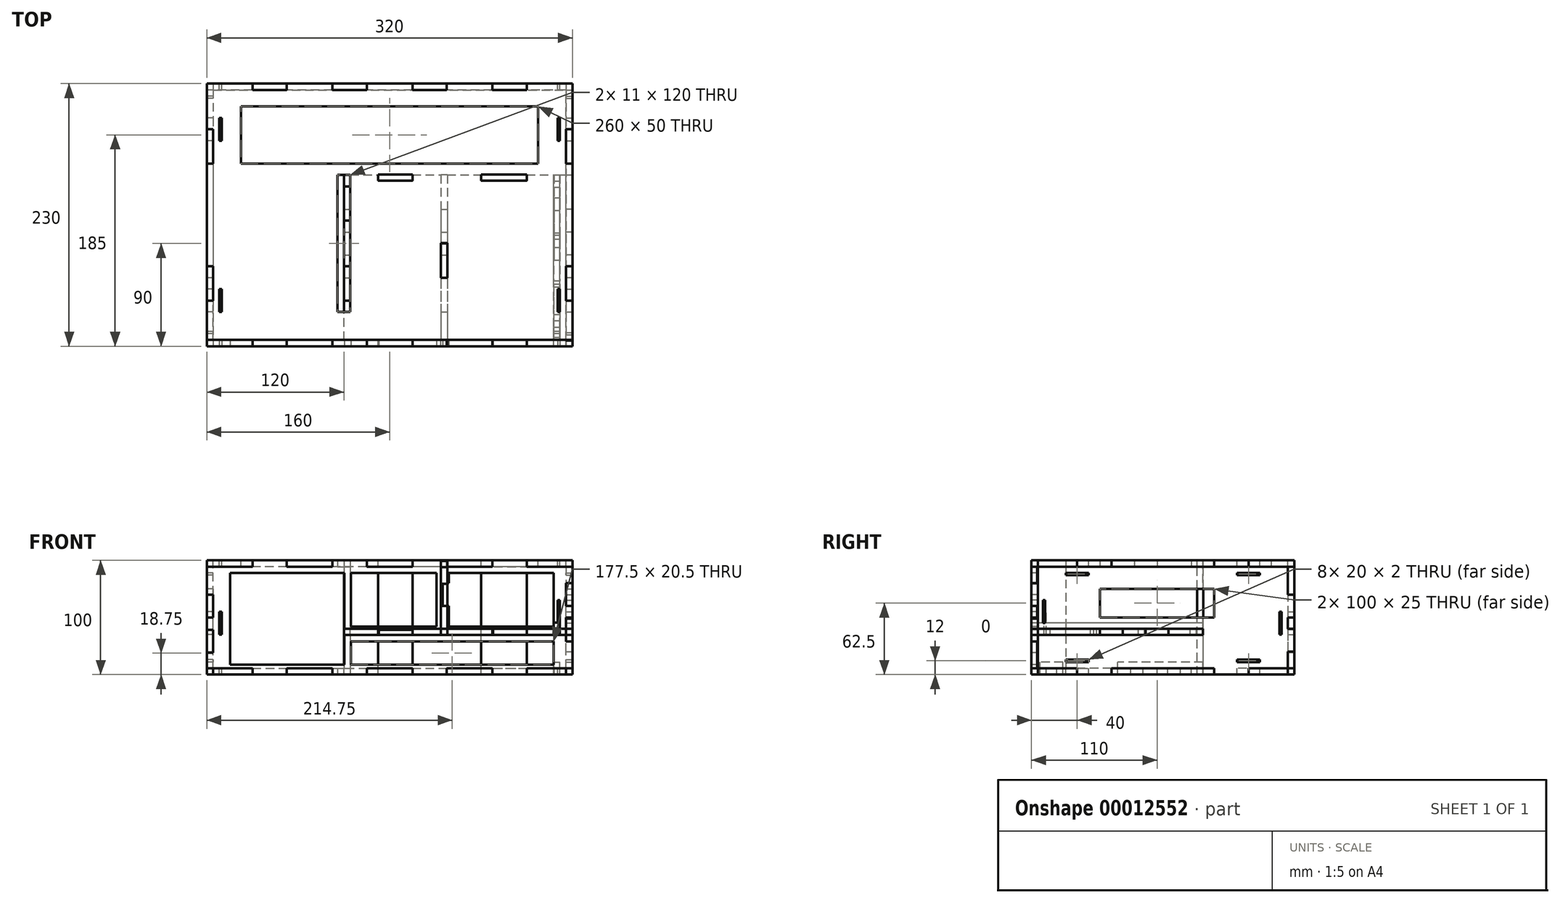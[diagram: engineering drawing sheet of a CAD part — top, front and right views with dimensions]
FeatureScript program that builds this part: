
annotation { "Feature Type Name" : "Feature", "Feature Type Description" : "" }
export const myFeature = defineFeature(function(context is Context, id is Id, definition is map)
    precondition{}
    {
        {
            var Q0;
            Q0=qCreatedBy(makeId("Top.planeOp"),FACE);
            var sketch = newSketch(context, id + "F0", { "sketchPlane" : qUnion([Q0])});
            skLineSegment(sketch, "E0.bottom", {"start": v(0, 0) * mm, "end": v(-320, 0) * mm});
            skLineSegment(sketch, "E0.top", {"start": v(0, 230) * mm, "end": v(-320, 230) * mm});
            skLineSegment(sketch, "E0.left", {"start": v(0, 0) * mm, "end": v(0, 230) * mm});
            skLineSegment(sketch, "E0.right", {"start": v(-320, 0) * mm, "end": v(-320, 230) * mm});
            skSolve(sketch);
        }
        {
            var Q0;
            Q0 = qSketchRegion(id + "F0", true);
            extrude(context, id + "F1", {"entities" : qUnion([Q0]), "depth" : 5.5 * mm});
        }
        {
            var Q0;
            Q0=makeQuery(id+"F1.opExtrude","CAP_FACE",FACE,{"disambiguationData":[OSD([sQuery(id+"F0.wireOp",EDGE,"E0.bottom"),sQuery(id+"F0.wireOp",EDGE,"E0.top"),sQuery(id+"F0.wireOp",EDGE,"E0.left"),sQuery(id+"F0.wireOp",EDGE,"E0.right")])],"isStart":false});
            var sketch = newSketch(context, id + "F2", { "sketchPlane" : qUnion([Q0])});
            skLineSegment(sketch, "E1.bottom", {"start": v(-280, 230) * mm, "end": v(-250, 230) * mm});
            skLineSegment(sketch, "E1.top", {"start": v(-280, 224.5) * mm, "end": v(-250, 224.5) * mm});
            skLineSegment(sketch, "E1.left", {"start": v(-280, 230) * mm, "end": v(-280, 224.5) * mm});
            skLineSegment(sketch, "E1.right", {"start": v(-250, 230) * mm, "end": v(-250, 224.5) * mm});
            skLineSegment(sketch, "E2.bottom", {"start": v(-70, 230) * mm, "end": v(-40, 230) * mm});
            skLineSegment(sketch, "E2.top", {"start": v(-70, 224.5) * mm, "end": v(-40, 224.5) * mm});
            skLineSegment(sketch, "E2.left", {"start": v(-70, 230) * mm, "end": v(-70, 224.5) * mm});
            skLineSegment(sketch, "E2.right", {"start": v(-40, 230) * mm, "end": v(-40, 224.5) * mm});
            skLineSegment(sketch, "E3.bottom", {"start": v(0, 190) * mm, "end": v(-5.5, 190) * mm});
            skLineSegment(sketch, "E3.top", {"start": v(0, 160) * mm, "end": v(-5.5, 160) * mm});
            skLineSegment(sketch, "E3.left", {"start": v(0, 190) * mm, "end": v(0, 160) * mm});
            skLineSegment(sketch, "E3.right", {"start": v(-5.5, 190) * mm, "end": v(-5.5, 160) * mm});
            skLineSegment(sketch, "E4.bottom", {"start": v(0, 70) * mm, "end": v(-5.5, 70) * mm});
            skLineSegment(sketch, "E4.top", {"start": v(0, 40) * mm, "end": v(-5.5, 40) * mm});
            skLineSegment(sketch, "E4.left", {"start": v(0, 70) * mm, "end": v(0, 40) * mm});
            skLineSegment(sketch, "E4.right", {"start": v(-5.5, 70) * mm, "end": v(-5.5, 40) * mm});
            skLineSegment(sketch, "E5.bottom", {"start": v(-320, 190) * mm, "end": v(-314.5, 190) * mm});
            skLineSegment(sketch, "E5.top", {"start": v(-320, 160) * mm, "end": v(-314.5, 160) * mm});
            skLineSegment(sketch, "E5.left", {"start": v(-320, 190) * mm, "end": v(-320, 160) * mm});
            skLineSegment(sketch, "E5.right", {"start": v(-314.5, 190) * mm, "end": v(-314.5, 160) * mm});
            skLineSegment(sketch, "E6.bottom", {"start": v(-320, 70) * mm, "end": v(-314.5, 70) * mm});
            skLineSegment(sketch, "E6.top", {"start": v(-320, 40) * mm, "end": v(-314.5, 40) * mm});
            skLineSegment(sketch, "E6.left", {"start": v(-320, 70) * mm, "end": v(-320, 40) * mm});
            skLineSegment(sketch, "E6.right", {"start": v(-314.5, 70) * mm, "end": v(-314.5, 40) * mm});
            skLineSegment(sketch, "E7.bottom", {"start": v(-210, 230) * mm, "end": v(-180, 230) * mm});
            skLineSegment(sketch, "E7.top", {"start": v(-210, 224.5) * mm, "end": v(-180, 224.5) * mm});
            skLineSegment(sketch, "E7.left", {"start": v(-210, 230) * mm, "end": v(-210, 224.5) * mm});
            skLineSegment(sketch, "E7.right", {"start": v(-180, 230) * mm, "end": v(-180, 224.5) * mm});
            skLineSegment(sketch, "E8.bottom", {"start": v(-140, 230) * mm, "end": v(-110, 230) * mm});
            skLineSegment(sketch, "E8.top", {"start": v(-140, 224.5) * mm, "end": v(-110, 224.5) * mm});
            skLineSegment(sketch, "E8.left", {"start": v(-140, 230) * mm, "end": v(-140, 224.5) * mm});
            skLineSegment(sketch, "E8.right", {"start": v(-110, 230) * mm, "end": v(-110, 224.5) * mm});
            skLineSegment(sketch, "E9.bottom", {"start": v(-309, 30) * mm, "end": v(-307, 30) * mm});
            skLineSegment(sketch, "E9.top", {"start": v(-309, 50) * mm, "end": v(-307, 50) * mm});
            skLineSegment(sketch, "E9.left", {"start": v(-309, 30) * mm, "end": v(-309, 50) * mm});
            skLineSegment(sketch, "E9.right", {"start": v(-307, 30) * mm, "end": v(-307, 50) * mm});
            skLineSegment(sketch, "E10.bottom", {"start": v(-13, 30) * mm, "end": v(-11, 30) * mm});
            skLineSegment(sketch, "E10.top", {"start": v(-13, 50) * mm, "end": v(-11, 50) * mm});
            skLineSegment(sketch, "E10.left", {"start": v(-13, 30) * mm, "end": v(-13, 50) * mm});
            skLineSegment(sketch, "E10.right", {"start": v(-11, 30) * mm, "end": v(-11, 50) * mm});
            skLineSegment(sketch, "E11.bottom", {"start": v(-11, 200) * mm, "end": v(-13, 200) * mm});
            skLineSegment(sketch, "E11.top", {"start": v(-11, 180) * mm, "end": v(-13, 180) * mm});
            skLineSegment(sketch, "E11.left", {"start": v(-11, 200) * mm, "end": v(-11, 180) * mm});
            skLineSegment(sketch, "E11.right", {"start": v(-13, 200) * mm, "end": v(-13, 180) * mm});
            skLineSegment(sketch, "E12.bottom", {"start": v(-309, 200) * mm, "end": v(-307, 200) * mm});
            skLineSegment(sketch, "E12.top", {"start": v(-309, 180) * mm, "end": v(-307, 180) * mm});
            skLineSegment(sketch, "E12.left", {"start": v(-309, 200) * mm, "end": v(-309, 180) * mm});
            skLineSegment(sketch, "E12.right", {"start": v(-307, 200) * mm, "end": v(-307, 180) * mm});
            skLineSegment(sketch, "E13.bottom", {"start": v(-280, 0) * mm, "end": v(-250, 0) * mm});
            skLineSegment(sketch, "E13.top", {"start": v(-280, 5.5) * mm, "end": v(-250, 5.5) * mm});
            skLineSegment(sketch, "E13.left", {"start": v(-280, 0) * mm, "end": v(-280, 5.5) * mm});
            skLineSegment(sketch, "E13.right", {"start": v(-250, 0) * mm, "end": v(-250, 5.5) * mm});
            skLineSegment(sketch, "E14.bottom", {"start": v(-210, 0) * mm, "end": v(-180, 0) * mm});
            skLineSegment(sketch, "E14.top", {"start": v(-210, 5.5) * mm, "end": v(-180, 5.5) * mm});
            skLineSegment(sketch, "E14.left", {"start": v(-210, 0) * mm, "end": v(-210, 5.5) * mm});
            skLineSegment(sketch, "E14.right", {"start": v(-180, 0) * mm, "end": v(-180, 5.5) * mm});
            skLineSegment(sketch, "E15.bottom", {"start": v(-140, 0) * mm, "end": v(-110, 0) * mm});
            skLineSegment(sketch, "E15.top", {"start": v(-140, 5.5) * mm, "end": v(-110, 5.5) * mm});
            skLineSegment(sketch, "E15.left", {"start": v(-140, 0) * mm, "end": v(-140, 5.5) * mm});
            skLineSegment(sketch, "E15.right", {"start": v(-110, 0) * mm, "end": v(-110, 5.5) * mm});
            skLineSegment(sketch, "E16.bottom", {"start": v(-70, 0) * mm, "end": v(-40, 0) * mm});
            skLineSegment(sketch, "E16.top", {"start": v(-70, 5.5) * mm, "end": v(-40, 5.5) * mm});
            skLineSegment(sketch, "E16.left", {"start": v(-70, 0) * mm, "end": v(-70, 5.5) * mm});
            skLineSegment(sketch, "E16.right", {"start": v(-40, 0) * mm, "end": v(-40, 5.5) * mm});
            skLineSegment(sketch, "E17.bottom", {"start": v(-200, 140) * mm, "end": v(-194.5, 140) * mm});
            skLineSegment(sketch, "E17.top", {"start": v(-200, 110) * mm, "end": v(-194.5, 110) * mm});
            skLineSegment(sketch, "E17.left", {"start": v(-200, 140) * mm, "end": v(-200, 110) * mm});
            skLineSegment(sketch, "E17.right", {"start": v(-194.5, 140) * mm, "end": v(-194.5, 110) * mm});
            skLineSegment(sketch, "E18.bottom", {"start": v(-200, 70) * mm, "end": v(-194.5, 70) * mm});
            skLineSegment(sketch, "E18.top", {"start": v(-200, 40) * mm, "end": v(-194.5, 40) * mm});
            skLineSegment(sketch, "E18.left", {"start": v(-200, 70) * mm, "end": v(-200, 40) * mm});
            skLineSegment(sketch, "E18.right", {"start": v(-194.5, 70) * mm, "end": v(-194.5, 40) * mm});
            skLineSegment(sketch, "E19.bottom", {"start": v(-170, 150.5) * mm, "end": v(-140, 150.5) * mm});
            skLineSegment(sketch, "E19.top", {"start": v(-170, 145) * mm, "end": v(-140, 145) * mm});
            skLineSegment(sketch, "E19.left", {"start": v(-170, 150.5) * mm, "end": v(-170, 145) * mm});
            skLineSegment(sketch, "E19.right", {"start": v(-140, 150.5) * mm, "end": v(-140, 145) * mm});
            skLineSegment(sketch, "E20.bottom", {"start": v(-80, 150.5) * mm, "end": v(-40, 150.5) * mm});
            skLineSegment(sketch, "E20.top", {"start": v(-80, 145) * mm, "end": v(-40, 145) * mm});
            skLineSegment(sketch, "E20.left", {"start": v(-80, 150.5) * mm, "end": v(-80, 145) * mm});
            skLineSegment(sketch, "E20.right", {"start": v(-40, 150.5) * mm, "end": v(-40, 145) * mm});
            skLineSegment(sketch, "E21.bottom", {"start": v(-16.5, 130) * mm, "end": v(-11, 130) * mm});
            skLineSegment(sketch, "E21.top", {"start": v(-16.5, 119) * mm, "end": v(-11, 119) * mm});
            skLineSegment(sketch, "E21.left", {"start": v(-16.5, 130) * mm, "end": v(-16.5, 119) * mm});
            skLineSegment(sketch, "E21.right", {"start": v(-11, 130) * mm, "end": v(-11, 119) * mm});
            skLineSegment(sketch, "E22.bottom", {"start": v(-16.5, 97.5) * mm, "end": v(-11, 97.5) * mm});
            skLineSegment(sketch, "E22.top", {"start": v(-16.5, 86.5) * mm, "end": v(-11, 86.5) * mm});
            skLineSegment(sketch, "E22.left", {"start": v(-16.5, 97.5) * mm, "end": v(-16.5, 86.5) * mm});
            skLineSegment(sketch, "E22.right", {"start": v(-11, 97.5) * mm, "end": v(-11, 86.5) * mm});
            skLineSegment(sketch, "E23.bottom", {"start": v(-16.5, 22) * mm, "end": v(-11, 22) * mm});
            skLineSegment(sketch, "E23.top", {"start": v(-16.5, 11) * mm, "end": v(-11, 11) * mm});
            skLineSegment(sketch, "E23.left", {"start": v(-16.5, 22) * mm, "end": v(-16.5, 11) * mm});
            skLineSegment(sketch, "E23.right", {"start": v(-11, 22) * mm, "end": v(-11, 11) * mm});
            skSolve(sketch);
        }
        {
            var Q0;
            Q0 = qSketchRegion(id + "F2", true);
            extrude(context, id + "F3", {"entities" : qUnion([Q0]), "operationType" : NewBodyOperationType.REMOVE, "oppositeDirection" : true, "depth" : 5.5 * mm});
        }
        {
            var Q0;
            {var subQ0=sQuery(id+"F0.wireOp",EDGE,"E0.top");Q0=makeQuery(id+"F3.boolean.opBoolean","SPLIT",FACE,{"disambiguationData":[TD([makeQuery(id+"F3.opExtrude","SWEPT_FACE",FACE,{"disambiguationData":[OSD([sQuery(id+"F2.wireOp",EDGE,"E2.left")])]})])],"derivedFrom":makeQuery(id+"F1.opExtrude","SWEPT_FACE",FACE,{"disambiguationData":[OSD([subQ0])]})});}
            var sketch = newSketch(context, id + "F4", { "sketchPlane" : qUnion([Q0])});
            skLineSegment(sketch, "E24.bottom", {"start": v(320, 0) * mm, "end": v(0, 0) * mm});
            skLineSegment(sketch, "E24.top", {"start": v(320, 100) * mm, "end": v(0, 100) * mm});
            skLineSegment(sketch, "E24.left", {"start": v(320, 0) * mm, "end": v(320, 100) * mm});
            skLineSegment(sketch, "E24.right", {"start": v(0, 0) * mm, "end": v(0, 100) * mm});
            skSolve(sketch);
        }
        {
            var Q0;
            Q0 = qSketchRegion(id + "F4", true);
            extrude(context, id + "F5", {"entities" : qUnion([Q0]), "oppositeDirection" : true, "depth" : 5.5 * mm});
        }
        {
            var Q0;
            Q0=makeQuery(id+"F5.opExtrude","CAP_FACE",FACE,{"disambiguationData":[OSD([sQuery(id+"F4.wireOp",EDGE,"E24.bottom"),sQuery(id+"F4.wireOp",EDGE,"E24.top"),sQuery(id+"F4.wireOp",EDGE,"E24.left"),sQuery(id+"F4.wireOp",EDGE,"E24.right")])],"isStart":true});
            var sketch = newSketch(context, id + "F6", { "sketchPlane" : qUnion([Q0])});
            skLineSegment(sketch, "E25.bottom", {"start": v(0, 0) * mm, "end": v(40, 0) * mm});
            skLineSegment(sketch, "E25.top", {"start": v(0, 5.5) * mm, "end": v(40, 5.5) * mm});
            skLineSegment(sketch, "E25.left", {"start": v(0, 0) * mm, "end": v(0, 5.5) * mm});
            skLineSegment(sketch, "E25.right", {"start": v(40, 0) * mm, "end": v(40, 5.5) * mm});
            skLineSegment(sketch, "E26.bottom", {"start": v(70, 0) * mm, "end": v(110, 0) * mm});
            skLineSegment(sketch, "E26.top", {"start": v(70, 5.5) * mm, "end": v(110, 5.5) * mm});
            skLineSegment(sketch, "E26.left", {"start": v(70, 0) * mm, "end": v(70, 5.5) * mm});
            skLineSegment(sketch, "E26.right", {"start": v(110, 0) * mm, "end": v(110, 5.5) * mm});
            skLineSegment(sketch, "E27.bottom", {"start": v(140, 0) * mm, "end": v(180, 0) * mm});
            skLineSegment(sketch, "E27.top", {"start": v(140, 5.5) * mm, "end": v(180, 5.5) * mm});
            skLineSegment(sketch, "E27.left", {"start": v(140, 0) * mm, "end": v(140, 5.5) * mm});
            skLineSegment(sketch, "E27.right", {"start": v(180, 0) * mm, "end": v(180, 5.5) * mm});
            skLineSegment(sketch, "E28.bottom", {"start": v(210, 0) * mm, "end": v(250, 0) * mm});
            skLineSegment(sketch, "E28.top", {"start": v(210, 5.5) * mm, "end": v(250, 5.5) * mm});
            skLineSegment(sketch, "E28.left", {"start": v(210, 0) * mm, "end": v(210, 5.5) * mm});
            skLineSegment(sketch, "E28.right", {"start": v(250, 0) * mm, "end": v(250, 5.5) * mm});
            skLineSegment(sketch, "E29.bottom", {"start": v(280, 0) * mm, "end": v(320, 0) * mm});
            skLineSegment(sketch, "E29.top", {"start": v(280, 5.5) * mm, "end": v(320, 5.5) * mm});
            skLineSegment(sketch, "E29.left", {"start": v(280, 0) * mm, "end": v(280, 5.5) * mm});
            skLineSegment(sketch, "E29.right", {"start": v(320, 0) * mm, "end": v(320, 5.5) * mm});
            skLineSegment(sketch, "E30.bottom", {"start": v(0, 70) * mm, "end": v(5.5, 70) * mm});
            skLineSegment(sketch, "E30.top", {"start": v(0, 50) * mm, "end": v(5.5, 50) * mm});
            skLineSegment(sketch, "E30.left", {"start": v(0, 70) * mm, "end": v(0, 50) * mm});
            skLineSegment(sketch, "E30.right", {"start": v(5.5, 70) * mm, "end": v(5.5, 50) * mm});
            skLineSegment(sketch, "E31.bottom", {"start": v(0, 40) * mm, "end": v(5.5, 40) * mm});
            skLineSegment(sketch, "E31.top", {"start": v(0, 20) * mm, "end": v(5.5, 20) * mm});
            skLineSegment(sketch, "E31.left", {"start": v(0, 40) * mm, "end": v(0, 20) * mm});
            skLineSegment(sketch, "E31.right", {"start": v(5.5, 40) * mm, "end": v(5.5, 20) * mm});
            skLineSegment(sketch, "E32.bottom", {"start": v(11, 55) * mm, "end": v(13, 55) * mm});
            skLineSegment(sketch, "E32.top", {"start": v(11, 35) * mm, "end": v(13, 35) * mm});
            skLineSegment(sketch, "E32.left", {"start": v(11, 55) * mm, "end": v(11, 35) * mm});
            skLineSegment(sketch, "E32.right", {"start": v(13, 55) * mm, "end": v(13, 35) * mm});
            skLineSegment(sketch, "E33.bottom", {"start": v(0, 100) * mm, "end": v(40, 100) * mm});
            skLineSegment(sketch, "E33.top", {"start": v(0, 94.5) * mm, "end": v(40, 94.5) * mm});
            skLineSegment(sketch, "E33.left", {"start": v(0, 100) * mm, "end": v(0, 94.5) * mm});
            skLineSegment(sketch, "E33.right", {"start": v(40, 100) * mm, "end": v(40, 94.5) * mm});
            skLineSegment(sketch, "E34.bottom", {"start": v(70, 100) * mm, "end": v(110, 100) * mm});
            skLineSegment(sketch, "E34.top", {"start": v(70, 94.5) * mm, "end": v(110, 94.5) * mm});
            skLineSegment(sketch, "E34.left", {"start": v(70, 100) * mm, "end": v(70, 94.5) * mm});
            skLineSegment(sketch, "E34.right", {"start": v(110, 100) * mm, "end": v(110, 94.5) * mm});
            skLineSegment(sketch, "E35.bottom", {"start": v(140, 100) * mm, "end": v(180, 100) * mm});
            skLineSegment(sketch, "E35.top", {"start": v(140, 94.5) * mm, "end": v(180, 94.5) * mm});
            skLineSegment(sketch, "E35.left", {"start": v(140, 100) * mm, "end": v(140, 94.5) * mm});
            skLineSegment(sketch, "E35.right", {"start": v(180, 100) * mm, "end": v(180, 94.5) * mm});
            skLineSegment(sketch, "E36.bottom", {"start": v(210, 100) * mm, "end": v(250, 100) * mm});
            skLineSegment(sketch, "E36.top", {"start": v(210, 94.5) * mm, "end": v(250, 94.5) * mm});
            skLineSegment(sketch, "E36.left", {"start": v(210, 100) * mm, "end": v(210, 94.5) * mm});
            skLineSegment(sketch, "E36.right", {"start": v(250, 100) * mm, "end": v(250, 94.5) * mm});
            skLineSegment(sketch, "E37.bottom", {"start": v(280, 100) * mm, "end": v(320, 100) * mm});
            skLineSegment(sketch, "E37.top", {"start": v(280, 94.5) * mm, "end": v(320, 94.5) * mm});
            skLineSegment(sketch, "E37.left", {"start": v(280, 100) * mm, "end": v(280, 94.5) * mm});
            skLineSegment(sketch, "E37.right", {"start": v(320, 100) * mm, "end": v(320, 94.5) * mm});
            skLineSegment(sketch, "E38.bottom", {"start": v(320, 70) * mm, "end": v(314.5, 70) * mm});
            skLineSegment(sketch, "E38.top", {"start": v(320, 50) * mm, "end": v(314.5, 50) * mm});
            skLineSegment(sketch, "E38.left", {"start": v(320, 70) * mm, "end": v(320, 50) * mm});
            skLineSegment(sketch, "E38.right", {"start": v(314.5, 70) * mm, "end": v(314.5, 50) * mm});
            skLineSegment(sketch, "E39.bottom", {"start": v(320, 40) * mm, "end": v(314.5, 40) * mm});
            skLineSegment(sketch, "E39.top", {"start": v(320, 20) * mm, "end": v(314.5, 20) * mm});
            skLineSegment(sketch, "E39.left", {"start": v(320, 40) * mm, "end": v(320, 20) * mm});
            skLineSegment(sketch, "E39.right", {"start": v(314.5, 40) * mm, "end": v(314.5, 20) * mm});
            skLineSegment(sketch, "E40.bottom", {"start": v(309, 55) * mm, "end": v(307, 55) * mm});
            skLineSegment(sketch, "E40.top", {"start": v(309, 35) * mm, "end": v(307, 35) * mm});
            skLineSegment(sketch, "E40.left", {"start": v(309, 55) * mm, "end": v(309, 35) * mm});
            skLineSegment(sketch, "E40.right", {"start": v(307, 55) * mm, "end": v(307, 35) * mm});
            skSolve(sketch);
        }
        {
            var Q0;
            Q0 = qSketchRegion(id + "F6", true);
            extrude(context, id + "F7", {"entities" : qUnion([Q0]), "operationType" : NewBodyOperationType.REMOVE, "oppositeDirection" : true, "depth" : 5.5 * mm});
        }
        {
            var Q0;
            {var subQ0=sQuery(id+"F0.wireOp",EDGE,"E0.left");var subQ1=sQuery(id+"F0.wireOp",EDGE,"E0.top");Q0=makeQuery(id+"F3.boolean.opBoolean","SPLIT",FACE,{"disambiguationData":[TD([makeQuery(id+"F1.opExtrude","SWEPT_FACE",FACE,{"disambiguationData":[OSD([subQ1])]})])],"derivedFrom":makeQuery(id+"F1.opExtrude","SWEPT_FACE",FACE,{"disambiguationData":[OSD([subQ0])]})});}
            var sketch = newSketch(context, id + "F8", { "sketchPlane" : qUnion([Q0])});
            skLineSegment(sketch, "E41.bottom", {"start": v(230, 0) * mm, "end": v(0, 0) * mm});
            skLineSegment(sketch, "E41.top", {"start": v(230, 100) * mm, "end": v(0, 100) * mm});
            skLineSegment(sketch, "E41.left", {"start": v(230, 0) * mm, "end": v(230, 100) * mm});
            skLineSegment(sketch, "E41.right", {"start": v(0, 0) * mm, "end": v(0, 100) * mm});
            skSolve(sketch);
        }
        {
            var Q0;
            Q0 = qSketchRegion(id + "F8", true);
            extrude(context, id + "F9", {"entities" : qUnion([Q0]), "oppositeDirection" : true, "depth" : 5.5 * mm});
        }
        {
            var Q0;
            Q0=makeQuery(id+"F9.opExtrude","CAP_FACE",FACE,{"disambiguationData":[OSD([sQuery(id+"F8.wireOp",EDGE,"E41.bottom"),sQuery(id+"F8.wireOp",EDGE,"E41.top"),sQuery(id+"F8.wireOp",EDGE,"E41.left"),sQuery(id+"F8.wireOp",EDGE,"E41.right")])],"isStart":true});
            var sketch = newSketch(context, id + "F10", { "sketchPlane" : qUnion([Q0])});
            skLineSegment(sketch, "E42.bottom", {"start": v(230, 100) * mm, "end": v(224.5, 100) * mm});
            skLineSegment(sketch, "E42.top", {"start": v(230, 70) * mm, "end": v(224.5, 70) * mm});
            skLineSegment(sketch, "E42.left", {"start": v(230, 100) * mm, "end": v(230, 70) * mm});
            skLineSegment(sketch, "E42.right", {"start": v(224.5, 100) * mm, "end": v(224.5, 70) * mm});
            skLineSegment(sketch, "E43.bottom", {"start": v(230, 50) * mm, "end": v(224.5, 50) * mm});
            skLineSegment(sketch, "E43.top", {"start": v(230, 40) * mm, "end": v(224.5, 40) * mm});
            skLineSegment(sketch, "E43.left", {"start": v(230, 50) * mm, "end": v(230, 40) * mm});
            skLineSegment(sketch, "E43.right", {"start": v(224.5, 50) * mm, "end": v(224.5, 40) * mm});
            skLineSegment(sketch, "E44.bottom", {"start": v(230, 0) * mm, "end": v(190, 0) * mm});
            skLineSegment(sketch, "E44.top", {"start": v(230, 5.5) * mm, "end": v(190, 5.5) * mm});
            skLineSegment(sketch, "E44.left", {"start": v(230, 0) * mm, "end": v(230, 5.5) * mm});
            skLineSegment(sketch, "E44.right", {"start": v(190, 0) * mm, "end": v(190, 5.5) * mm});
            skLineSegment(sketch, "E45.bottom", {"start": v(160, 0) * mm, "end": v(70, 0) * mm});
            skLineSegment(sketch, "E45.top", {"start": v(160, 5.5) * mm, "end": v(70, 5.5) * mm});
            skLineSegment(sketch, "E45.left", {"start": v(160, 0) * mm, "end": v(160, 5.5) * mm});
            skLineSegment(sketch, "E45.right", {"start": v(70, 0) * mm, "end": v(70, 5.5) * mm});
            skLineSegment(sketch, "E46.bottom", {"start": v(0, 0) * mm, "end": v(40, 0) * mm});
            skLineSegment(sketch, "E46.top", {"start": v(0, 5.5) * mm, "end": v(40, 5.5) * mm});
            skLineSegment(sketch, "E46.left", {"start": v(0, 0) * mm, "end": v(0, 5.5) * mm});
            skLineSegment(sketch, "E46.right", {"start": v(40, 0) * mm, "end": v(40, 5.5) * mm});
            skLineSegment(sketch, "E47.bottom", {"start": v(230, 5.5) * mm, "end": v(224.5, 5.5) * mm});
            skLineSegment(sketch, "E47.top", {"start": v(230, 20) * mm, "end": v(224.5, 20) * mm});
            skLineSegment(sketch, "E47.left", {"start": v(230, 5.5) * mm, "end": v(230, 20) * mm});
            skLineSegment(sketch, "E47.right", {"start": v(224.5, 5.5) * mm, "end": v(224.5, 20) * mm});
            skLineSegment(sketch, "E48.bottom", {"start": v(0, 5.5) * mm, "end": v(5, 5.5) * mm});
            skLineSegment(sketch, "E48.top", {"start": v(0, 30) * mm, "end": v(5, 30) * mm});
            skLineSegment(sketch, "E48.left", {"start": v(0, 5.5) * mm, "end": v(0, 30) * mm});
            skLineSegment(sketch, "E48.right", {"start": v(5, 5.5) * mm, "end": v(5, 30) * mm});
            skLineSegment(sketch, "E49.bottom", {"start": v(0, 50) * mm, "end": v(5, 50) * mm});
            skLineSegment(sketch, "E49.top", {"start": v(0, 60) * mm, "end": v(5, 60) * mm});
            skLineSegment(sketch, "E49.left", {"start": v(0, 50) * mm, "end": v(0, 60) * mm});
            skLineSegment(sketch, "E49.right", {"start": v(5, 50) * mm, "end": v(5, 60) * mm});
            skLineSegment(sketch, "E50.bottom", {"start": v(0, 100) * mm, "end": v(5, 100) * mm});
            skLineSegment(sketch, "E50.top", {"start": v(0, 80) * mm, "end": v(5, 80) * mm});
            skLineSegment(sketch, "E50.left", {"start": v(0, 100) * mm, "end": v(0, 80) * mm});
            skLineSegment(sketch, "E50.right", {"start": v(5, 100) * mm, "end": v(5, 80) * mm});
            skLineSegment(sketch, "E51.bottom", {"start": v(217, 35) * mm, "end": v(219, 35) * mm});
            skLineSegment(sketch, "E51.top", {"start": v(217, 55) * mm, "end": v(219, 55) * mm});
            skLineSegment(sketch, "E51.left", {"start": v(217, 35) * mm, "end": v(217, 55) * mm});
            skLineSegment(sketch, "E51.right", {"start": v(219, 35) * mm, "end": v(219, 55) * mm});
            skLineSegment(sketch, "E52.bottom", {"start": v(12, 45) * mm, "end": v(10, 45) * mm});
            skLineSegment(sketch, "E52.top", {"start": v(12, 65) * mm, "end": v(10, 65) * mm});
            skLineSegment(sketch, "E52.left", {"start": v(12, 45) * mm, "end": v(12, 65) * mm});
            skLineSegment(sketch, "E52.right", {"start": v(10, 45) * mm, "end": v(10, 65) * mm});
            skLineSegment(sketch, "E53.bottom", {"start": v(5, 94.5) * mm, "end": v(40, 94.5) * mm});
            skLineSegment(sketch, "E53.top", {"start": v(5, 100) * mm, "end": v(40, 100) * mm});
            skLineSegment(sketch, "E53.left", {"start": v(5, 94.5) * mm, "end": v(5, 100) * mm});
            skLineSegment(sketch, "E53.right", {"start": v(40, 94.5) * mm, "end": v(40, 100) * mm});
            skLineSegment(sketch, "E54.bottom", {"start": v(70, 100) * mm, "end": v(160, 100) * mm});
            skLineSegment(sketch, "E54.top", {"start": v(70, 94.5) * mm, "end": v(160, 94.5) * mm});
            skLineSegment(sketch, "E54.left", {"start": v(70, 100) * mm, "end": v(70, 94.5) * mm});
            skLineSegment(sketch, "E54.right", {"start": v(160, 100) * mm, "end": v(160, 94.5) * mm});
            skLineSegment(sketch, "E55.bottom", {"start": v(190, 100) * mm, "end": v(224.5, 100) * mm});
            skLineSegment(sketch, "E55.top", {"start": v(190, 94.5) * mm, "end": v(224.5, 94.5) * mm});
            skLineSegment(sketch, "E55.left", {"start": v(190, 100) * mm, "end": v(190, 94.5) * mm});
            skLineSegment(sketch, "E55.right", {"start": v(224.5, 100) * mm, "end": v(224.5, 94.5) * mm});
            skLineSegment(sketch, "E56.bottom", {"start": v(30, 13) * mm, "end": v(50, 13) * mm});
            skLineSegment(sketch, "E56.top", {"start": v(30, 11) * mm, "end": v(50, 11) * mm});
            skLineSegment(sketch, "E56.left", {"start": v(30, 13) * mm, "end": v(30, 11) * mm});
            skLineSegment(sketch, "E56.right", {"start": v(50, 13) * mm, "end": v(50, 11) * mm});
            skLineSegment(sketch, "E57.bottom", {"start": v(200, 11) * mm, "end": v(180, 11) * mm});
            skLineSegment(sketch, "E57.top", {"start": v(200, 13) * mm, "end": v(180, 13) * mm});
            skLineSegment(sketch, "E57.left", {"start": v(200, 11) * mm, "end": v(200, 13) * mm});
            skLineSegment(sketch, "E57.right", {"start": v(180, 11) * mm, "end": v(180, 13) * mm});
            skLineSegment(sketch, "E58.bottom", {"start": v(200, 87) * mm, "end": v(180, 87) * mm});
            skLineSegment(sketch, "E58.top", {"start": v(200, 89) * mm, "end": v(180, 89) * mm});
            skLineSegment(sketch, "E58.left", {"start": v(200, 87) * mm, "end": v(200, 89) * mm});
            skLineSegment(sketch, "E58.right", {"start": v(180, 87) * mm, "end": v(180, 89) * mm});
            skLineSegment(sketch, "E59.bottom", {"start": v(50, 87) * mm, "end": v(30, 87) * mm});
            skLineSegment(sketch, "E59.top", {"start": v(50, 89) * mm, "end": v(30, 89) * mm});
            skLineSegment(sketch, "E59.left", {"start": v(50, 87) * mm, "end": v(50, 89) * mm});
            skLineSegment(sketch, "E59.right", {"start": v(30, 87) * mm, "end": v(30, 89) * mm});
            skLineSegment(sketch, "E60.bottom", {"start": v(60, 75) * mm, "end": v(160, 75) * mm});
            skLineSegment(sketch, "E60.top", {"start": v(60, 50) * mm, "end": v(160, 50) * mm});
            skLineSegment(sketch, "E60.left", {"start": v(60, 75) * mm, "end": v(60, 50) * mm});
            skLineSegment(sketch, "E60.right", {"start": v(160, 75) * mm, "end": v(160, 50) * mm});
            skLineSegment(sketch, "E61.bottom", {"start": v(60, 40) * mm, "end": v(80, 40) * mm});
            skLineSegment(sketch, "E61.top", {"start": v(60, 34.5) * mm, "end": v(80, 34.5) * mm});
            skLineSegment(sketch, "E61.left", {"start": v(60, 40) * mm, "end": v(60, 34.5) * mm});
            skLineSegment(sketch, "E61.right", {"start": v(80, 40) * mm, "end": v(80, 34.5) * mm});
            skLineSegment(sketch, "E62.bottom", {"start": v(100, 40) * mm, "end": v(120, 40) * mm});
            skLineSegment(sketch, "E62.top", {"start": v(100, 34.5) * mm, "end": v(120, 34.5) * mm});
            skLineSegment(sketch, "E62.left", {"start": v(100, 40) * mm, "end": v(100, 34.5) * mm});
            skLineSegment(sketch, "E62.right", {"start": v(120, 40) * mm, "end": v(120, 34.5) * mm});
            skSolve(sketch);
        }
        {
            var Q0;
            Q0 = qSketchRegion(id + "F10", true);
            extrude(context, id + "F11", {"entities" : qUnion([Q0]), "operationType" : NewBodyOperationType.REMOVE, "oppositeDirection" : true, "depth" : 5.5 * mm});
        }
        {
            var Q0;
            {var subQ0=sQuery(id+"F0.wireOp",EDGE,"E0.right");var subQ1=sQuery(id+"F0.wireOp",EDGE,"E0.top");Q0=makeQuery(id+"F3.boolean.opBoolean","SPLIT",FACE,{"disambiguationData":[TD([makeQuery(id+"F1.opExtrude","SWEPT_FACE",FACE,{"disambiguationData":[OSD([subQ1])]})])],"derivedFrom":makeQuery(id+"F1.opExtrude","SWEPT_FACE",FACE,{"disambiguationData":[OSD([subQ0])]})});}
            var sketch = newSketch(context, id + "F12", { "sketchPlane" : qUnion([Q0])});
            skLineSegment(sketch, "E63.bottom", {"start": v(-230, 0) * mm, "end": v(0, 0) * mm});
            skLineSegment(sketch, "E63.top", {"start": v(-230, 100) * mm, "end": v(0, 100) * mm});
            skLineSegment(sketch, "E63.left", {"start": v(-230, 0) * mm, "end": v(-230, 100) * mm});
            skLineSegment(sketch, "E63.right", {"start": v(0, 0) * mm, "end": v(0, 100) * mm});
            skSolve(sketch);
        }
        {
            var Q0;
            Q0 = qSketchRegion(id + "F12", true);
            extrude(context, id + "F13", {"entities" : qUnion([Q0]), "oppositeDirection" : true, "depth" : 5.5 * mm});
        }
        {
            var Q0;
            Q0=makeQuery(id+"F13.opExtrude","CAP_FACE",FACE,{"disambiguationData":[OSD([sQuery(id+"F12.wireOp",EDGE,"E63.bottom"),sQuery(id+"F12.wireOp",EDGE,"E63.top"),sQuery(id+"F12.wireOp",EDGE,"E63.left"),sQuery(id+"F12.wireOp",EDGE,"E63.right")])],"isStart":true});
            var sketch = newSketch(context, id + "F14", { "sketchPlane" : qUnion([Q0])});
            skLineSegment(sketch, "E64.bottom", {"start": v(-230, 0) * mm, "end": v(-190, 0) * mm});
            skLineSegment(sketch, "E64.top", {"start": v(-230, 5.5) * mm, "end": v(-190, 5.5) * mm});
            skLineSegment(sketch, "E64.left", {"start": v(-230, 0) * mm, "end": v(-230, 5.5) * mm});
            skLineSegment(sketch, "E64.right", {"start": v(-190, 0) * mm, "end": v(-190, 5.5) * mm});
            skLineSegment(sketch, "E65.bottom", {"start": v(0, 0) * mm, "end": v(-40, 0) * mm});
            skLineSegment(sketch, "E65.top", {"start": v(0, 5.5) * mm, "end": v(-40, 5.5) * mm});
            skLineSegment(sketch, "E65.left", {"start": v(0, 0) * mm, "end": v(0, 5.5) * mm});
            skLineSegment(sketch, "E65.right", {"start": v(-40, 0) * mm, "end": v(-40, 5.5) * mm});
            skLineSegment(sketch, "E66.bottom", {"start": v(0, 100) * mm, "end": v(-40, 100) * mm});
            skLineSegment(sketch, "E66.top", {"start": v(0, 94.5) * mm, "end": v(-40, 94.5) * mm});
            skLineSegment(sketch, "E66.left", {"start": v(0, 100) * mm, "end": v(0, 94.5) * mm});
            skLineSegment(sketch, "E66.right", {"start": v(-40, 100) * mm, "end": v(-40, 94.5) * mm});
            skLineSegment(sketch, "E67.bottom", {"start": v(-230, 100) * mm, "end": v(-190, 100) * mm});
            skLineSegment(sketch, "E67.top", {"start": v(-230, 94.5) * mm, "end": v(-190, 94.5) * mm});
            skLineSegment(sketch, "E67.left", {"start": v(-230, 100) * mm, "end": v(-230, 94.5) * mm});
            skLineSegment(sketch, "E67.right", {"start": v(-190, 100) * mm, "end": v(-190, 94.5) * mm});
            skLineSegment(sketch, "E68.bottom", {"start": v(-160, 0) * mm, "end": v(-70, 0) * mm});
            skLineSegment(sketch, "E68.top", {"start": v(-160, 5.5) * mm, "end": v(-70, 5.5) * mm});
            skLineSegment(sketch, "E68.left", {"start": v(-160, 0) * mm, "end": v(-160, 5.5) * mm});
            skLineSegment(sketch, "E68.right", {"start": v(-70, 0) * mm, "end": v(-70, 5.5) * mm});
            skLineSegment(sketch, "E69.bottom", {"start": v(-70, 100) * mm, "end": v(-160, 100) * mm});
            skLineSegment(sketch, "E69.top", {"start": v(-70, 94.5) * mm, "end": v(-160, 94.5) * mm});
            skLineSegment(sketch, "E69.left", {"start": v(-70, 100) * mm, "end": v(-70, 94.5) * mm});
            skLineSegment(sketch, "E69.right", {"start": v(-160, 100) * mm, "end": v(-160, 94.5) * mm});
            skLineSegment(sketch, "E70.bottom", {"start": v(-200, 13) * mm, "end": v(-180, 13) * mm});
            skLineSegment(sketch, "E70.top", {"start": v(-200, 11) * mm, "end": v(-180, 11) * mm});
            skLineSegment(sketch, "E70.left", {"start": v(-200, 13) * mm, "end": v(-200, 11) * mm});
            skLineSegment(sketch, "E70.right", {"start": v(-180, 13) * mm, "end": v(-180, 11) * mm});
            skLineSegment(sketch, "E71.bottom", {"start": v(-30, 11) * mm, "end": v(-50, 11) * mm});
            skLineSegment(sketch, "E71.top", {"start": v(-30, 13) * mm, "end": v(-50, 13) * mm});
            skLineSegment(sketch, "E71.left", {"start": v(-30, 11) * mm, "end": v(-30, 13) * mm});
            skLineSegment(sketch, "E71.right", {"start": v(-50, 11) * mm, "end": v(-50, 13) * mm});
            skLineSegment(sketch, "E72.bottom", {"start": v(-50, 87) * mm, "end": v(-30, 87) * mm});
            skLineSegment(sketch, "E72.top", {"start": v(-50, 89) * mm, "end": v(-30, 89) * mm});
            skLineSegment(sketch, "E72.left", {"start": v(-50, 87) * mm, "end": v(-50, 89) * mm});
            skLineSegment(sketch, "E72.right", {"start": v(-30, 87) * mm, "end": v(-30, 89) * mm});
            skLineSegment(sketch, "E73.bottom", {"start": v(-180, 87) * mm, "end": v(-200, 87) * mm});
            skLineSegment(sketch, "E73.top", {"start": v(-180, 89) * mm, "end": v(-200, 89) * mm});
            skLineSegment(sketch, "E73.left", {"start": v(-180, 87) * mm, "end": v(-180, 89) * mm});
            skLineSegment(sketch, "E73.right", {"start": v(-200, 87) * mm, "end": v(-200, 89) * mm});
            skLineSegment(sketch, "E74.bottom", {"start": v(-230, 5.5) * mm, "end": v(-224.5, 5.5) * mm});
            skLineSegment(sketch, "E74.top", {"start": v(-230, 19) * mm, "end": v(-224.5, 19) * mm});
            skLineSegment(sketch, "E74.left", {"start": v(-230, 5.5) * mm, "end": v(-230, 19) * mm});
            skLineSegment(sketch, "E74.right", {"start": v(-224.5, 5.5) * mm, "end": v(-224.5, 19) * mm});
            skLineSegment(sketch, "E75.bottom", {"start": v(0, 5.5) * mm, "end": v(-5.5, 5.5) * mm});
            skLineSegment(sketch, "E75.top", {"start": v(0, 19) * mm, "end": v(-5.5, 19) * mm});
            skLineSegment(sketch, "E75.left", {"start": v(0, 5.5) * mm, "end": v(0, 19) * mm});
            skLineSegment(sketch, "E75.right", {"start": v(-5.5, 5.5) * mm, "end": v(-5.5, 19) * mm});
            skLineSegment(sketch, "E76.bottom", {"start": v(-230, 39) * mm, "end": v(-224.5, 39) * mm});
            skLineSegment(sketch, "E76.top", {"start": v(-230, 50) * mm, "end": v(-224.5, 50) * mm});
            skLineSegment(sketch, "E76.left", {"start": v(-230, 39) * mm, "end": v(-230, 50) * mm});
            skLineSegment(sketch, "E76.right", {"start": v(-224.5, 39) * mm, "end": v(-224.5, 50) * mm});
            skLineSegment(sketch, "E77.bottom", {"start": v(-11, 35) * mm, "end": v(-13, 35) * mm});
            skLineSegment(sketch, "E77.top", {"start": v(-11, 55) * mm, "end": v(-13, 55) * mm});
            skLineSegment(sketch, "E77.left", {"start": v(-11, 35) * mm, "end": v(-11, 55) * mm});
            skLineSegment(sketch, "E77.right", {"start": v(-13, 35) * mm, "end": v(-13, 55) * mm});
            skLineSegment(sketch, "E78.bottom", {"start": v(-219, 35) * mm, "end": v(-217, 35) * mm});
            skLineSegment(sketch, "E78.top", {"start": v(-219, 55) * mm, "end": v(-217, 55) * mm});
            skLineSegment(sketch, "E78.left", {"start": v(-219, 35) * mm, "end": v(-219, 55) * mm});
            skLineSegment(sketch, "E78.right", {"start": v(-217, 35) * mm, "end": v(-217, 55) * mm});
            skLineSegment(sketch, "E79.bottom", {"start": v(-230, 70) * mm, "end": v(-224.5, 70) * mm});
            skLineSegment(sketch, "E79.top", {"start": v(-230, 94.5) * mm, "end": v(-224.5, 94.5) * mm});
            skLineSegment(sketch, "E79.left", {"start": v(-230, 70) * mm, "end": v(-230, 94.5) * mm});
            skLineSegment(sketch, "E79.right", {"start": v(-224.5, 70) * mm, "end": v(-224.5, 94.5) * mm});
            skLineSegment(sketch, "E80.bottom", {"start": v(0, 70) * mm, "end": v(-5.5, 70) * mm});
            skLineSegment(sketch, "E80.top", {"start": v(0, 94.5) * mm, "end": v(-5.5, 94.5) * mm});
            skLineSegment(sketch, "E80.left", {"start": v(0, 70) * mm, "end": v(0, 94.5) * mm});
            skLineSegment(sketch, "E80.right", {"start": v(-5.5, 70) * mm, "end": v(-5.5, 94.5) * mm});
            skLineSegment(sketch, "E81.bottom", {"start": v(0, 50) * mm, "end": v(-5.5, 50) * mm});
            skLineSegment(sketch, "E81.top", {"start": v(0, 39) * mm, "end": v(-5.5, 39) * mm});
            skLineSegment(sketch, "E81.left", {"start": v(0, 39) * mm, "end": v(0, 50) * mm});
            skLineSegment(sketch, "E81.right", {"start": v(-5.5, 39) * mm, "end": v(-5.5, 50) * mm});
            skLineSegment(sketch, "E82.bottom", {"start": v(-160, 75) * mm, "end": v(-60, 75) * mm});
            skLineSegment(sketch, "E82.top", {"start": v(-160, 50) * mm, "end": v(-60, 50) * mm});
            skLineSegment(sketch, "E82.left", {"start": v(-160, 75) * mm, "end": v(-160, 50) * mm});
            skLineSegment(sketch, "E82.right", {"start": v(-60, 75) * mm, "end": v(-60, 50) * mm});
            skSolve(sketch);
        }
        {
            var Q0;
            Q0 = qSketchRegion(id + "F14", true);
            extrude(context, id + "F15", {"entities" : qUnion([Q0]), "operationType" : NewBodyOperationType.REMOVE, "oppositeDirection" : true, "depth" : 5.5 * mm});
        }
        {
            var Q0;
            {var subQ0=sQuery(id+"F4.wireOp",EDGE,"E24.top");Q0=makeQuery(id+"F7.boolean.opBoolean","SPLIT",FACE,{"disambiguationData":[TD([makeQuery(id+"F7.opExtrude","SWEPT_FACE",FACE,{"disambiguationData":[OSD([sQuery(id+"F6.wireOp",EDGE,"E33.right")])]})])],"derivedFrom":makeQuery(id+"F5.opExtrude","SWEPT_FACE",FACE,{"disambiguationData":[OSD([subQ0])]})});}
            var sketch = newSketch(context, id + "F16", { "sketchPlane" : qUnion([Q0])});
            skLineSegment(sketch, "E83.bottom", {"start": v(0, 230) * mm, "end": v(-320, 230) * mm});
            skLineSegment(sketch, "E83.top", {"start": v(0, 0) * mm, "end": v(-320, 0) * mm});
            skLineSegment(sketch, "E83.left", {"start": v(0, 230) * mm, "end": v(0, 0) * mm});
            skLineSegment(sketch, "E83.right", {"start": v(-320, 230) * mm, "end": v(-320, 0) * mm});
            skSolve(sketch);
        }
        {
            var Q0;
            Q0 = qSketchRegion(id + "F16", true);
            extrude(context, id + "F17", {"entities" : qUnion([Q0]), "oppositeDirection" : true, "depth" : 5.5 * mm});
        }
        {
            var Q0;
            Q0=makeQuery(id+"F17.opExtrude","CAP_FACE",FACE,{"disambiguationData":[OSD([sQuery(id+"F16.wireOp",EDGE,"E83.bottom"),sQuery(id+"F16.wireOp",EDGE,"E83.top"),sQuery(id+"F16.wireOp",EDGE,"E83.left"),sQuery(id+"F16.wireOp",EDGE,"E83.right")])],"isStart":true});
            var sketch = newSketch(context, id + "F18", { "sketchPlane" : qUnion([Q0])});
            skLineSegment(sketch, "E84.bottom", {"start": v(0, 40) * mm, "end": v(-5.5, 40) * mm});
            skLineSegment(sketch, "E84.top", {"start": v(0, 70) * mm, "end": v(-5.5, 70) * mm});
            skLineSegment(sketch, "E84.left", {"start": v(0, 40) * mm, "end": v(0, 70) * mm});
            skLineSegment(sketch, "E84.right", {"start": v(-5.5, 40) * mm, "end": v(-5.5, 70) * mm});
            skLineSegment(sketch, "E85.bottom", {"start": v(-320, 40) * mm, "end": v(-314.5, 40) * mm});
            skLineSegment(sketch, "E85.top", {"start": v(-320, 70) * mm, "end": v(-314.5, 70) * mm});
            skLineSegment(sketch, "E85.left", {"start": v(-320, 40) * mm, "end": v(-320, 70) * mm});
            skLineSegment(sketch, "E85.right", {"start": v(-314.5, 40) * mm, "end": v(-314.5, 70) * mm});
            skLineSegment(sketch, "E86.bottom", {"start": v(-320, 160) * mm, "end": v(-314.5, 160) * mm});
            skLineSegment(sketch, "E86.top", {"start": v(-320, 190) * mm, "end": v(-314.5, 190) * mm});
            skLineSegment(sketch, "E86.left", {"start": v(-320, 160) * mm, "end": v(-320, 190) * mm});
            skLineSegment(sketch, "E86.right", {"start": v(-314.5, 160) * mm, "end": v(-314.5, 190) * mm});
            skLineSegment(sketch, "E87.bottom", {"start": v(0, 160) * mm, "end": v(-5.5, 160) * mm});
            skLineSegment(sketch, "E87.top", {"start": v(0, 190) * mm, "end": v(-5.5, 190) * mm});
            skLineSegment(sketch, "E87.left", {"start": v(0, 160) * mm, "end": v(0, 190) * mm});
            skLineSegment(sketch, "E87.right", {"start": v(-5.5, 160) * mm, "end": v(-5.5, 190) * mm});
            skLineSegment(sketch, "E88.bottom", {"start": v(-11, 50) * mm, "end": v(-13, 50) * mm});
            skLineSegment(sketch, "E88.top", {"start": v(-11, 30) * mm, "end": v(-13, 30) * mm});
            skLineSegment(sketch, "E88.left", {"start": v(-11, 50) * mm, "end": v(-11, 30) * mm});
            skLineSegment(sketch, "E88.right", {"start": v(-13, 50) * mm, "end": v(-13, 30) * mm});
            skLineSegment(sketch, "E89.bottom", {"start": v(-309, 30) * mm, "end": v(-307, 30) * mm});
            skLineSegment(sketch, "E89.top", {"start": v(-309, 50) * mm, "end": v(-307, 50) * mm});
            skLineSegment(sketch, "E89.left", {"start": v(-309, 30) * mm, "end": v(-309, 50) * mm});
            skLineSegment(sketch, "E89.right", {"start": v(-307, 30) * mm, "end": v(-307, 50) * mm});
            skLineSegment(sketch, "E90.bottom", {"start": v(-309, 180) * mm, "end": v(-307, 180) * mm});
            skLineSegment(sketch, "E90.top", {"start": v(-309, 200) * mm, "end": v(-307, 200) * mm});
            skLineSegment(sketch, "E90.left", {"start": v(-309, 180) * mm, "end": v(-309, 200) * mm});
            skLineSegment(sketch, "E90.right", {"start": v(-307, 180) * mm, "end": v(-307, 200) * mm});
            skLineSegment(sketch, "E91.bottom", {"start": v(-13, 180) * mm, "end": v(-11, 180) * mm});
            skLineSegment(sketch, "E91.top", {"start": v(-13, 200) * mm, "end": v(-11, 200) * mm});
            skLineSegment(sketch, "E91.left", {"start": v(-13, 180) * mm, "end": v(-13, 200) * mm});
            skLineSegment(sketch, "E91.right", {"start": v(-11, 180) * mm, "end": v(-11, 200) * mm});
            skLineSegment(sketch, "E92.bottom", {"start": v(-40, 230) * mm, "end": v(-70, 230) * mm});
            skLineSegment(sketch, "E92.top", {"start": v(-40, 224.5) * mm, "end": v(-70, 224.5) * mm});
            skLineSegment(sketch, "E92.left", {"start": v(-40, 230) * mm, "end": v(-40, 224.5) * mm});
            skLineSegment(sketch, "E92.right", {"start": v(-70, 230) * mm, "end": v(-70, 224.5) * mm});
            skLineSegment(sketch, "E93.bottom", {"start": v(-110, 230) * mm, "end": v(-140, 230) * mm});
            skLineSegment(sketch, "E93.top", {"start": v(-110, 224.5) * mm, "end": v(-140, 224.5) * mm});
            skLineSegment(sketch, "E93.left", {"start": v(-110, 230) * mm, "end": v(-110, 224.5) * mm});
            skLineSegment(sketch, "E93.right", {"start": v(-140, 230) * mm, "end": v(-140, 224.5) * mm});
            skLineSegment(sketch, "E94.bottom", {"start": v(-180, 230) * mm, "end": v(-210, 230) * mm});
            skLineSegment(sketch, "E94.top", {"start": v(-180, 224.5) * mm, "end": v(-210, 224.5) * mm});
            skLineSegment(sketch, "E94.left", {"start": v(-180, 230) * mm, "end": v(-180, 224.5) * mm});
            skLineSegment(sketch, "E94.right", {"start": v(-210, 230) * mm, "end": v(-210, 224.5) * mm});
            skLineSegment(sketch, "E95.bottom", {"start": v(-250, 230) * mm, "end": v(-280, 230) * mm});
            skLineSegment(sketch, "E95.top", {"start": v(-250, 224.5) * mm, "end": v(-280, 224.5) * mm});
            skLineSegment(sketch, "E95.left", {"start": v(-250, 230) * mm, "end": v(-250, 224.5) * mm});
            skLineSegment(sketch, "E95.right", {"start": v(-280, 230) * mm, "end": v(-280, 224.5) * mm});
            skLineSegment(sketch, "E96.bottom", {"start": v(-40, 0) * mm, "end": v(-70, 0) * mm});
            skLineSegment(sketch, "E96.top", {"start": v(-40, 5.5) * mm, "end": v(-70, 5.5) * mm});
            skLineSegment(sketch, "E96.left", {"start": v(-40, 0) * mm, "end": v(-40, 5.5) * mm});
            skLineSegment(sketch, "E96.right", {"start": v(-70, 0) * mm, "end": v(-70, 5.5) * mm});
            skLineSegment(sketch, "E97.bottom", {"start": v(-110, 0) * mm, "end": v(-140, 0) * mm});
            skLineSegment(sketch, "E97.top", {"start": v(-110, 5.5) * mm, "end": v(-140, 5.5) * mm});
            skLineSegment(sketch, "E97.left", {"start": v(-110, 0) * mm, "end": v(-110, 5.5) * mm});
            skLineSegment(sketch, "E97.right", {"start": v(-140, 0) * mm, "end": v(-140, 5.5) * mm});
            skLineSegment(sketch, "E98.bottom", {"start": v(-180, 0) * mm, "end": v(-210, 0) * mm});
            skLineSegment(sketch, "E98.top", {"start": v(-180, 5.5) * mm, "end": v(-210, 5.5) * mm});
            skLineSegment(sketch, "E98.left", {"start": v(-180, 0) * mm, "end": v(-180, 5.5) * mm});
            skLineSegment(sketch, "E98.right", {"start": v(-210, 0) * mm, "end": v(-210, 5.5) * mm});
            skLineSegment(sketch, "E99.bottom", {"start": v(-250, 0) * mm, "end": v(-280, 0) * mm});
            skLineSegment(sketch, "E99.top", {"start": v(-250, 5.5) * mm, "end": v(-280, 5.5) * mm});
            skLineSegment(sketch, "E99.left", {"start": v(-250, 0) * mm, "end": v(-250, 5.5) * mm});
            skLineSegment(sketch, "E99.right", {"start": v(-280, 0) * mm, "end": v(-280, 5.5) * mm});
            skLineSegment(sketch, "E100.bottom", {"start": v(-290, 210) * mm, "end": v(-30, 210) * mm});
            skLineSegment(sketch, "E100.top", {"start": v(-290, 160) * mm, "end": v(-30, 160) * mm});
            skLineSegment(sketch, "E100.left", {"start": v(-290, 210) * mm, "end": v(-290, 160) * mm});
            skLineSegment(sketch, "E100.right", {"start": v(-30, 210) * mm, "end": v(-30, 160) * mm});
            skLineSegment(sketch, "E101.bottom", {"start": v(-200, 40) * mm, "end": v(-194.5, 40) * mm});
            skLineSegment(sketch, "E101.top", {"start": v(-200, 70) * mm, "end": v(-194.5, 70) * mm});
            skLineSegment(sketch, "E101.left", {"start": v(-200, 40) * mm, "end": v(-200, 70) * mm});
            skLineSegment(sketch, "E101.right", {"start": v(-194.5, 40) * mm, "end": v(-194.5, 70) * mm});
            skLineSegment(sketch, "E102.bottom", {"start": v(-200, 110) * mm, "end": v(-194.5, 110) * mm});
            skLineSegment(sketch, "E102.top", {"start": v(-200, 140) * mm, "end": v(-194.5, 140) * mm});
            skLineSegment(sketch, "E102.left", {"start": v(-200, 110) * mm, "end": v(-200, 140) * mm});
            skLineSegment(sketch, "E102.right", {"start": v(-194.5, 110) * mm, "end": v(-194.5, 140) * mm});
            skLineSegment(sketch, "E103.bottom", {"start": v(-140, 150.5) * mm, "end": v(-170, 150.5) * mm});
            skLineSegment(sketch, "E103.top", {"start": v(-140, 145) * mm, "end": v(-170, 145) * mm});
            skLineSegment(sketch, "E103.left", {"start": v(-140, 150.5) * mm, "end": v(-140, 145) * mm});
            skLineSegment(sketch, "E103.right", {"start": v(-170, 150.5) * mm, "end": v(-170, 145) * mm});
            skLineSegment(sketch, "E104.bottom", {"start": v(-80, 150.5) * mm, "end": v(-40, 150.5) * mm});
            skLineSegment(sketch, "E104.top", {"start": v(-80, 145) * mm, "end": v(-40, 145) * mm});
            skLineSegment(sketch, "E104.left", {"start": v(-80, 150.5) * mm, "end": v(-80, 145) * mm});
            skLineSegment(sketch, "E104.right", {"start": v(-40, 150.5) * mm, "end": v(-40, 145) * mm});
            skLineSegment(sketch, "E105.bottom", {"start": v(-115, 90.5) * mm, "end": v(-109.5, 90.5) * mm});
            skLineSegment(sketch, "E105.top", {"start": v(-115, 60) * mm, "end": v(-109.5, 60) * mm});
            skLineSegment(sketch, "E105.left", {"start": v(-115, 90.5) * mm, "end": v(-115, 60) * mm});
            skLineSegment(sketch, "E105.right", {"start": v(-109.5, 90.5) * mm, "end": v(-109.5, 60) * mm});
            skSolve(sketch);
        }
        {
            var Q0;
            Q0 = qSketchRegion(id + "F18", true);
            extrude(context, id + "F19", {"entities" : qUnion([Q0]), "operationType" : NewBodyOperationType.REMOVE, "oppositeDirection" : true, "depth" : 5.5 * mm});
        }
        {
            var Q0;
            {var subQ0=sQuery(id+"F16.wireOp",EDGE,"E83.top");var subQ1=sQuery(id+"F16.wireOp",EDGE,"E83.right");Q0=makeQuery(id+"F19.boolean.opBoolean","SPLIT",FACE,{"disambiguationData":[TD([makeQuery(id+"F17.opExtrude","SWEPT_FACE",FACE,{"disambiguationData":[OSD([subQ1])]})])],"derivedFrom":makeQuery(id+"F17.opExtrude","SWEPT_FACE",FACE,{"disambiguationData":[OSD([subQ0])]})});}
            var sketch = newSketch(context, id + "F20", { "sketchPlane" : qUnion([Q0])});
            skLineSegment(sketch, "E106.bottom", {"start": v(-320, 100) * mm, "end": v(0, 100) * mm});
            skLineSegment(sketch, "E106.top", {"start": v(-320, 0) * mm, "end": v(0, 0) * mm});
            skLineSegment(sketch, "E106.left", {"start": v(-320, 100) * mm, "end": v(-320, 0) * mm});
            skLineSegment(sketch, "E106.right", {"start": v(0, 100) * mm, "end": v(0, 0) * mm});
            skSolve(sketch);
        }
        {
            var Q0;
            Q0 = qSketchRegion(id + "F20", true);
            extrude(context, id + "F21", {"entities" : qUnion([Q0]), "oppositeDirection" : true, "depth" : 5.5 * mm});
        }
        {
            var Q0;
            Q0=makeQuery(id+"F21.opExtrude","CAP_FACE",FACE,{"disambiguationData":[OSD([sQuery(id+"F20.wireOp",EDGE,"E106.bottom"),sQuery(id+"F20.wireOp",EDGE,"E106.top"),sQuery(id+"F20.wireOp",EDGE,"E106.left"),sQuery(id+"F20.wireOp",EDGE,"E106.right")])],"isStart":true});
            var sketch = newSketch(context, id + "F22", { "sketchPlane" : qUnion([Q0])});
            skLineSegment(sketch, "E107.bottom", {"start": v(-320, 100) * mm, "end": v(-280, 100) * mm});
            skLineSegment(sketch, "E107.top", {"start": v(-320, 94.5) * mm, "end": v(-280, 94.5) * mm});
            skLineSegment(sketch, "E107.left", {"start": v(-320, 100) * mm, "end": v(-320, 94.5) * mm});
            skLineSegment(sketch, "E107.right", {"start": v(-280, 100) * mm, "end": v(-280, 94.5) * mm});
            skLineSegment(sketch, "E108.bottom", {"start": v(-320, 0) * mm, "end": v(-280, 0) * mm});
            skLineSegment(sketch, "E108.top", {"start": v(-320, 5.5) * mm, "end": v(-280, 5.5) * mm});
            skLineSegment(sketch, "E108.left", {"start": v(-320, 0) * mm, "end": v(-320, 5.5) * mm});
            skLineSegment(sketch, "E108.right", {"start": v(-280, 0) * mm, "end": v(-280, 5.5) * mm});
            skLineSegment(sketch, "E109.bottom", {"start": v(-250, 100) * mm, "end": v(-210, 100) * mm});
            skLineSegment(sketch, "E109.top", {"start": v(-250, 94.5) * mm, "end": v(-210, 94.5) * mm});
            skLineSegment(sketch, "E109.left", {"start": v(-250, 100) * mm, "end": v(-250, 94.5) * mm});
            skLineSegment(sketch, "E109.right", {"start": v(-210, 100) * mm, "end": v(-210, 94.5) * mm});
            skLineSegment(sketch, "E110.bottom", {"start": v(-250, 0) * mm, "end": v(-210, 0) * mm});
            skLineSegment(sketch, "E110.top", {"start": v(-250, 5.5) * mm, "end": v(-210, 5.5) * mm});
            skLineSegment(sketch, "E110.left", {"start": v(-250, 0) * mm, "end": v(-250, 5.5) * mm});
            skLineSegment(sketch, "E110.right", {"start": v(-210, 0) * mm, "end": v(-210, 5.5) * mm});
            skLineSegment(sketch, "E111.bottom", {"start": v(-180, 100) * mm, "end": v(-140, 100) * mm});
            skLineSegment(sketch, "E111.top", {"start": v(-180, 94.5) * mm, "end": v(-140, 94.5) * mm});
            skLineSegment(sketch, "E111.left", {"start": v(-180, 100) * mm, "end": v(-180, 94.5) * mm});
            skLineSegment(sketch, "E111.right", {"start": v(-140, 100) * mm, "end": v(-140, 94.5) * mm});
            skLineSegment(sketch, "E112.bottom", {"start": v(-180, 0) * mm, "end": v(-140, 0) * mm});
            skLineSegment(sketch, "E112.top", {"start": v(-180, 5.5) * mm, "end": v(-140, 5.5) * mm});
            skLineSegment(sketch, "E112.left", {"start": v(-180, 0) * mm, "end": v(-180, 5.5) * mm});
            skLineSegment(sketch, "E112.right", {"start": v(-140, 0) * mm, "end": v(-140, 5.5) * mm});
            skLineSegment(sketch, "E113.bottom", {"start": v(-110, 100) * mm, "end": v(-70, 100) * mm});
            skLineSegment(sketch, "E113.top", {"start": v(-110, 94.5) * mm, "end": v(-70, 94.5) * mm});
            skLineSegment(sketch, "E113.left", {"start": v(-110, 100) * mm, "end": v(-110, 94.5) * mm});
            skLineSegment(sketch, "E113.right", {"start": v(-70, 100) * mm, "end": v(-70, 94.5) * mm});
            skLineSegment(sketch, "E114.bottom", {"start": v(-40, 100) * mm, "end": v(0, 100) * mm});
            skLineSegment(sketch, "E114.top", {"start": v(-40, 94.5) * mm, "end": v(0, 94.5) * mm});
            skLineSegment(sketch, "E114.left", {"start": v(-40, 100) * mm, "end": v(-40, 94.5) * mm});
            skLineSegment(sketch, "E114.right", {"start": v(0, 100) * mm, "end": v(0, 94.5) * mm});
            skLineSegment(sketch, "E115.bottom", {"start": v(0, 0) * mm, "end": v(-40, 0) * mm});
            skLineSegment(sketch, "E115.top", {"start": v(0, 5.5) * mm, "end": v(-40, 5.5) * mm});
            skLineSegment(sketch, "E115.left", {"start": v(0, 0) * mm, "end": v(0, 5.5) * mm});
            skLineSegment(sketch, "E115.right", {"start": v(-40, 0) * mm, "end": v(-40, 5.5) * mm});
            skLineSegment(sketch, "E116.bottom", {"start": v(-70, 0) * mm, "end": v(-110, 0) * mm});
            skLineSegment(sketch, "E116.top", {"start": v(-70, 5.5) * mm, "end": v(-110, 5.5) * mm});
            skLineSegment(sketch, "E116.left", {"start": v(-70, 0) * mm, "end": v(-70, 5.5) * mm});
            skLineSegment(sketch, "E116.right", {"start": v(-110, 0) * mm, "end": v(-110, 5.5) * mm});
            skLineSegment(sketch, "E117.bottom", {"start": v(-320, 19) * mm, "end": v(-314.5, 19) * mm});
            skLineSegment(sketch, "E117.top", {"start": v(-320, 39) * mm, "end": v(-314.5, 39) * mm});
            skLineSegment(sketch, "E117.left", {"start": v(-320, 19) * mm, "end": v(-320, 39) * mm});
            skLineSegment(sketch, "E117.right", {"start": v(-314.5, 19) * mm, "end": v(-314.5, 39) * mm});
            skLineSegment(sketch, "E118.bottom", {"start": v(-320, 50) * mm, "end": v(-314.5, 50) * mm});
            skLineSegment(sketch, "E118.top", {"start": v(-320, 70) * mm, "end": v(-314.5, 70) * mm});
            skLineSegment(sketch, "E118.left", {"start": v(-320, 50) * mm, "end": v(-320, 70) * mm});
            skLineSegment(sketch, "E118.right", {"start": v(-314.5, 50) * mm, "end": v(-314.5, 70) * mm});
            skLineSegment(sketch, "E119.bottom", {"start": v(-309, 35) * mm, "end": v(-307, 35) * mm});
            skLineSegment(sketch, "E119.top", {"start": v(-309, 55) * mm, "end": v(-307, 55) * mm});
            skLineSegment(sketch, "E119.left", {"start": v(-309, 35) * mm, "end": v(-309, 55) * mm});
            skLineSegment(sketch, "E119.right", {"start": v(-307, 35) * mm, "end": v(-307, 55) * mm});
            skLineSegment(sketch, "E120.bottom", {"start": v(0, 29) * mm, "end": v(-5.5, 29) * mm});
            skLineSegment(sketch, "E120.top", {"start": v(0, 49) * mm, "end": v(-5.5, 49) * mm});
            skLineSegment(sketch, "E120.left", {"start": v(0, 29) * mm, "end": v(0, 49) * mm});
            skLineSegment(sketch, "E120.right", {"start": v(-5.5, 29) * mm, "end": v(-5.5, 49) * mm});
            skLineSegment(sketch, "E121.bottom", {"start": v(0, 60) * mm, "end": v(-5.5, 60) * mm});
            skLineSegment(sketch, "E121.top", {"start": v(0, 80) * mm, "end": v(-5.5, 80) * mm});
            skLineSegment(sketch, "E121.left", {"start": v(0, 60) * mm, "end": v(0, 80) * mm});
            skLineSegment(sketch, "E121.right", {"start": v(-5.5, 60) * mm, "end": v(-5.5, 80) * mm});
            skLineSegment(sketch, "E122.bottom", {"start": v(-11, 45) * mm, "end": v(-13, 45) * mm});
            skLineSegment(sketch, "E122.top", {"start": v(-11, 65) * mm, "end": v(-13, 65) * mm});
            skLineSegment(sketch, "E122.left", {"start": v(-11, 45) * mm, "end": v(-11, 65) * mm});
            skLineSegment(sketch, "E122.right", {"start": v(-13, 45) * mm, "end": v(-13, 65) * mm});
            skLineSegment(sketch, "E123.bottom", {"start": v(-299.5, 8.5) * mm, "end": v(-199.5, 8.5) * mm});
            skLineSegment(sketch, "E123.top", {"start": v(-299.5, 89) * mm, "end": v(-199.5, 89) * mm});
            skLineSegment(sketch, "E123.left", {"start": v(-299.5, 8.5) * mm, "end": v(-299.5, 89) * mm});
            skLineSegment(sketch, "E123.right", {"start": v(-199.5, 8.5) * mm, "end": v(-199.5, 89) * mm});
            skLineSegment(sketch, "E124.bottom", {"start": v(-194, 89) * mm, "end": v(-119, 89) * mm});
            skLineSegment(sketch, "E124.top", {"start": v(-194, 42) * mm, "end": v(-119, 42) * mm});
            skLineSegment(sketch, "E124.left", {"start": v(-194, 89) * mm, "end": v(-194, 42) * mm});
            skLineSegment(sketch, "E124.right", {"start": v(-119, 89) * mm, "end": v(-119, 42) * mm});
            skLineSegment(sketch, "E125.bottom", {"start": v(-194, 8.5) * mm, "end": v(-16.5, 8.5) * mm});
            skLineSegment(sketch, "E125.top", {"start": v(-194, 29) * mm, "end": v(-16.5, 29) * mm});
            skLineSegment(sketch, "E125.left", {"start": v(-194, 8.5) * mm, "end": v(-194, 29) * mm});
            skLineSegment(sketch, "E125.right", {"start": v(-16.5, 8.5) * mm, "end": v(-16.5, 29) * mm});
            skLineSegment(sketch, "E126.bottom", {"start": v(-69.5, 40) * mm, "end": v(-39.5, 40) * mm});
            skLineSegment(sketch, "E126.top", {"start": v(-69.5, 34.5) * mm, "end": v(-39.5, 34.5) * mm});
            skLineSegment(sketch, "E126.left", {"start": v(-69.5, 40) * mm, "end": v(-69.5, 34.5) * mm});
            skLineSegment(sketch, "E126.right", {"start": v(-39.5, 40) * mm, "end": v(-39.5, 34.5) * mm});
            skLineSegment(sketch, "E127.bottom", {"start": v(-169.5, 39) * mm, "end": v(-139.5, 39) * mm});
            skLineSegment(sketch, "E127.top", {"start": v(-169.5, 34.5) * mm, "end": v(-139.5, 34.5) * mm});
            skLineSegment(sketch, "E127.left", {"start": v(-169.5, 39) * mm, "end": v(-169.5, 34.5) * mm});
            skLineSegment(sketch, "E127.right", {"start": v(-139.5, 39) * mm, "end": v(-139.5, 34.5) * mm});
            skLineSegment(sketch, "E128.bottom", {"start": v(-108, 42) * mm, "end": v(-16.5, 42) * mm});
            skLineSegment(sketch, "E128.top", {"start": v(-108, 89) * mm, "end": v(-16.5, 89) * mm});
            skLineSegment(sketch, "E128.left", {"start": v(-108, 42) * mm, "end": v(-108, 89) * mm});
            skLineSegment(sketch, "E128.right", {"start": v(-16.5, 42) * mm, "end": v(-16.5, 89) * mm});
            skLineSegment(sketch, "E129.bottom", {"start": v(-113.5, 80) * mm, "end": v(-108, 80) * mm});
            skLineSegment(sketch, "E129.top", {"start": v(-113.5, 60) * mm, "end": v(-108, 60) * mm});
            skLineSegment(sketch, "E129.left", {"start": v(-113.5, 80) * mm, "end": v(-113.5, 60) * mm});
            skLineSegment(sketch, "E129.right", {"start": v(-108, 80) * mm, "end": v(-108, 60) * mm});
            skSolve(sketch);
        }
        {
            var Q0;
            Q0 = qSketchRegion(id + "F22", true);
            extrude(context, id + "F23", {"entities" : qUnion([Q0]), "operationType" : NewBodyOperationType.REMOVE, "oppositeDirection" : true, "depth" : 5.5 * mm});
        }
        {
            var Q0;
            Q0=makeQuery(id+"F19.boolean.opBoolean","COPY",FACE,{"derivedFrom":makeQuery(id+"F19.opExtrude","SWEPT_FACE",FACE,{"disambiguationData":[OSD([sQuery(id+"F18.wireOp",EDGE,"E101.left")])]})});
            var sketch = newSketch(context, id + "F24", { "sketchPlane" : qUnion([Q0])});
            skLineSegment(sketch, "E130.bottom", {"start": v(30, 100) * mm, "end": v(150, 100) * mm});
            skLineSegment(sketch, "E130.top", {"start": v(30, 0) * mm, "end": v(150, 0) * mm});
            skLineSegment(sketch, "E130.left", {"start": v(30, 100) * mm, "end": v(30, 0) * mm});
            skLineSegment(sketch, "E130.right", {"start": v(150, 100) * mm, "end": v(150, 0) * mm});
            skSolve(sketch);
        }
        {
            var Q0;
            Q0 = qSketchRegion(id + "F24", true);
            extrude(context, id + "F25", {"entities" : qUnion([Q0]), "depth" : 5.5 * mm});
        }
        {
            var Q0;
            Q0=makeQuery(id+"F25.opExtrude","CAP_FACE",FACE,{"disambiguationData":[OSD([sQuery(id+"F24.wireOp",EDGE,"E130.bottom"),sQuery(id+"F24.wireOp",EDGE,"E130.top"),sQuery(id+"F24.wireOp",EDGE,"E130.left"),sQuery(id+"F24.wireOp",EDGE,"E130.right")])],"isStart":false});
            var sketch = newSketch(context, id + "F26", { "sketchPlane" : qUnion([Q0])});
            skLineSegment(sketch, "E131.bottom", {"start": v(30, 0) * mm, "end": v(40, 0) * mm});
            skLineSegment(sketch, "E131.top", {"start": v(30, 5.5) * mm, "end": v(40, 5.5) * mm});
            skLineSegment(sketch, "E131.left", {"start": v(30, 0) * mm, "end": v(30, 5.5) * mm});
            skLineSegment(sketch, "E131.right", {"start": v(40, 0) * mm, "end": v(40, 5.5) * mm});
            skLineSegment(sketch, "E132.bottom", {"start": v(70, 0) * mm, "end": v(110, 0) * mm});
            skLineSegment(sketch, "E132.top", {"start": v(70, 5.5) * mm, "end": v(110, 5.5) * mm});
            skLineSegment(sketch, "E132.left", {"start": v(70, 0) * mm, "end": v(70, 5.5) * mm});
            skLineSegment(sketch, "E132.right", {"start": v(110, 0) * mm, "end": v(110, 5.5) * mm});
            skLineSegment(sketch, "E133.bottom", {"start": v(140, 0) * mm, "end": v(150, 0) * mm});
            skLineSegment(sketch, "E133.top", {"start": v(140, 5.5) * mm, "end": v(150, 5.5) * mm});
            skLineSegment(sketch, "E133.left", {"start": v(140, 0) * mm, "end": v(140, 5.5) * mm});
            skLineSegment(sketch, "E133.right", {"start": v(150, 0) * mm, "end": v(150, 5.5) * mm});
            skLineSegment(sketch, "E134.bottom", {"start": v(30, 100) * mm, "end": v(40, 100) * mm});
            skLineSegment(sketch, "E134.top", {"start": v(30, 94.5) * mm, "end": v(40, 94.5) * mm});
            skLineSegment(sketch, "E134.left", {"start": v(30, 100) * mm, "end": v(30, 94.5) * mm});
            skLineSegment(sketch, "E134.right", {"start": v(40, 100) * mm, "end": v(40, 94.5) * mm});
            skLineSegment(sketch, "E135.bottom", {"start": v(70, 100) * mm, "end": v(110, 100) * mm});
            skLineSegment(sketch, "E135.top", {"start": v(70, 94.5) * mm, "end": v(110, 94.5) * mm});
            skLineSegment(sketch, "E135.left", {"start": v(70, 100) * mm, "end": v(70, 94.5) * mm});
            skLineSegment(sketch, "E135.right", {"start": v(110, 100) * mm, "end": v(110, 94.5) * mm});
            skLineSegment(sketch, "E136.bottom", {"start": v(150, 100) * mm, "end": v(140, 100) * mm});
            skLineSegment(sketch, "E136.top", {"start": v(150, 94.5) * mm, "end": v(140, 94.5) * mm});
            skLineSegment(sketch, "E136.left", {"start": v(150, 100) * mm, "end": v(150, 94.5) * mm});
            skLineSegment(sketch, "E136.right", {"start": v(140, 100) * mm, "end": v(140, 94.5) * mm});
            skLineSegment(sketch, "E137.bottom", {"start": v(60, 34.5) * mm, "end": v(80, 34.5) * mm});
            skLineSegment(sketch, "E137.top", {"start": v(60, 40) * mm, "end": v(80, 40) * mm});
            skLineSegment(sketch, "E137.left", {"start": v(60, 34.5) * mm, "end": v(60, 40) * mm});
            skLineSegment(sketch, "E137.right", {"start": v(80, 34.5) * mm, "end": v(80, 40) * mm});
            skLineSegment(sketch, "E138.bottom", {"start": v(100, 34.5) * mm, "end": v(120, 34.5) * mm});
            skLineSegment(sketch, "E138.top", {"start": v(100, 40) * mm, "end": v(120, 40) * mm});
            skLineSegment(sketch, "E138.left", {"start": v(100, 34.5) * mm, "end": v(100, 40) * mm});
            skLineSegment(sketch, "E138.right", {"start": v(120, 34.5) * mm, "end": v(120, 40) * mm});
            skSolve(sketch);
        }
        {
            var Q0;
            Q0 = qSketchRegion(id + "F26", true);
            var Q1;
            Q1=makeQuery(id+"F25.opExtrude","CAP_FACE",FACE,{"disambiguationData":[OSD([sQuery(id+"F24.wireOp",EDGE,"E130.bottom"),sQuery(id+"F24.wireOp",EDGE,"E130.top"),sQuery(id+"F24.wireOp",EDGE,"E130.left"),sQuery(id+"F24.wireOp",EDGE,"E130.right")])],"isStart":true});
            extrude(context, id + "F27", {"entities" : qUnion([Q0, Q1]), "operationType" : NewBodyOperationType.REMOVE, "oppositeDirection" : true, "depth" : 5.5 * mm});
        }
        {
            var Q0;
            Q0=makeQuery(id+"F27.boolean.opBoolean","COPY",FACE,{"derivedFrom":makeQuery(id+"F27.opExtrude","SWEPT_FACE",FACE,{"disambiguationData":[OSD([sQuery(id+"F26.wireOp",EDGE,"E137.bottom")])]})});
            var sketch = newSketch(context, id + "F28", { "sketchPlane" : qUnion([Q0])});
            skLineSegment(sketch, "E139.bottom", {"start": v(-200, 0) * mm, "end": v(0, 0) * mm});
            skLineSegment(sketch, "E139.top", {"start": v(-200, 150) * mm, "end": v(0, 150) * mm});
            skLineSegment(sketch, "E139.left", {"start": v(-200, 0) * mm, "end": v(-200, 150) * mm});
            skLineSegment(sketch, "E139.right", {"start": v(0, 0) * mm, "end": v(0, 150) * mm});
            skSolve(sketch);
        }
        {
            var Q0;
            Q0 = qSketchRegion(id + "F28", true);
            extrude(context, id + "F29", {"entities" : qUnion([Q0]), "depth" : 5.5 * mm});
        }
        {
            var Q0;
            Q0=makeQuery(id+"F29.opExtrude","CAP_FACE",FACE,{"disambiguationData":[OSD([sQuery(id+"F28.wireOp",EDGE,"E139.bottom"),sQuery(id+"F28.wireOp",EDGE,"E139.top"),sQuery(id+"F28.wireOp",EDGE,"E139.left"),sQuery(id+"F28.wireOp",EDGE,"E139.right")])],"isStart":false});
            var sketch = newSketch(context, id + "F30", { "sketchPlane" : qUnion([Q0])});
            skLineSegment(sketch, "E140.bottom", {"start": v(-200, 0) * mm, "end": v(-170, 0) * mm});
            skLineSegment(sketch, "E140.top", {"start": v(-200, 5.5) * mm, "end": v(-170, 5.5) * mm});
            skLineSegment(sketch, "E140.left", {"start": v(-200, 0) * mm, "end": v(-200, 5.5) * mm});
            skLineSegment(sketch, "E140.right", {"start": v(-170, 0) * mm, "end": v(-170, 5.5) * mm});
            skLineSegment(sketch, "E141.bottom", {"start": v(-200, 30) * mm, "end": v(-194.5, 30) * mm});
            skLineSegment(sketch, "E141.top", {"start": v(-200, 60) * mm, "end": v(-194.5, 60) * mm});
            skLineSegment(sketch, "E141.left", {"start": v(-200, 30) * mm, "end": v(-200, 60) * mm});
            skLineSegment(sketch, "E141.right", {"start": v(-194.5, 30) * mm, "end": v(-194.5, 60) * mm});
            skLineSegment(sketch, "E142.bottom", {"start": v(-200, 80) * mm, "end": v(-194.5, 80) * mm});
            skLineSegment(sketch, "E142.top", {"start": v(-200, 100) * mm, "end": v(-194.5, 100) * mm});
            skLineSegment(sketch, "E142.left", {"start": v(-200, 80) * mm, "end": v(-200, 100) * mm});
            skLineSegment(sketch, "E142.right", {"start": v(-194.5, 80) * mm, "end": v(-194.5, 100) * mm});
            skLineSegment(sketch, "E143.bottom", {"start": v(-200, 120) * mm, "end": v(-194.5, 120) * mm});
            skLineSegment(sketch, "E143.top", {"start": v(-200, 150) * mm, "end": v(-194.5, 150) * mm});
            skLineSegment(sketch, "E143.left", {"start": v(-200, 120) * mm, "end": v(-200, 150) * mm});
            skLineSegment(sketch, "E143.right", {"start": v(-194.5, 120) * mm, "end": v(-194.5, 150) * mm});
            skLineSegment(sketch, "E144.bottom", {"start": v(-140, 0) * mm, "end": v(-70, 0) * mm});
            skLineSegment(sketch, "E144.top", {"start": v(-140, 5.5) * mm, "end": v(-70, 5.5) * mm});
            skLineSegment(sketch, "E144.left", {"start": v(-140, 0) * mm, "end": v(-140, 5.5) * mm});
            skLineSegment(sketch, "E144.right", {"start": v(-70, 0) * mm, "end": v(-70, 5.5) * mm});
            skLineSegment(sketch, "E145.bottom", {"start": v(-40, 0) * mm, "end": v(0, 0) * mm});
            skLineSegment(sketch, "E145.top", {"start": v(-40, 5.5) * mm, "end": v(0, 5.5) * mm});
            skLineSegment(sketch, "E145.left", {"start": v(-40, 0) * mm, "end": v(-40, 5.5) * mm});
            skLineSegment(sketch, "E145.right", {"start": v(0, 0) * mm, "end": v(0, 5.5) * mm});
            skLineSegment(sketch, "E146.bottom", {"start": v(0, 5.5) * mm, "end": v(-5.5, 5.5) * mm});
            skLineSegment(sketch, "E146.top", {"start": v(0, 60) * mm, "end": v(-5.5, 60) * mm});
            skLineSegment(sketch, "E146.left", {"start": v(0, 5.5) * mm, "end": v(0, 60) * mm});
            skLineSegment(sketch, "E146.right", {"start": v(-5.5, 5.5) * mm, "end": v(-5.5, 60) * mm});
            skLineSegment(sketch, "E147.bottom", {"start": v(0, 80) * mm, "end": v(-5.5, 80) * mm});
            skLineSegment(sketch, "E147.top", {"start": v(0, 100) * mm, "end": v(-5.5, 100) * mm});
            skLineSegment(sketch, "E147.left", {"start": v(0, 80) * mm, "end": v(0, 100) * mm});
            skLineSegment(sketch, "E147.right", {"start": v(-5.5, 80) * mm, "end": v(-5.5, 100) * mm});
            skLineSegment(sketch, "E148.bottom", {"start": v(0, 120) * mm, "end": v(-5.5, 120) * mm});
            skLineSegment(sketch, "E148.top", {"start": v(0, 150) * mm, "end": v(-5.5, 150) * mm});
            skLineSegment(sketch, "E148.left", {"start": v(0, 120) * mm, "end": v(0, 150) * mm});
            skLineSegment(sketch, "E148.right", {"start": v(-5.5, 120) * mm, "end": v(-5.5, 150) * mm});
            skLineSegment(sketch, "E149.bottom", {"start": v(-115, 100) * mm, "end": v(-109.5, 100) * mm});
            skLineSegment(sketch, "E149.top", {"start": v(-115, 80) * mm, "end": v(-109.5, 80) * mm});
            skLineSegment(sketch, "E149.left", {"start": v(-115, 100) * mm, "end": v(-115, 80) * mm});
            skLineSegment(sketch, "E149.right", {"start": v(-109.5, 100) * mm, "end": v(-109.5, 80) * mm});
            skLineSegment(sketch, "E150.bottom", {"start": v(-115, 60) * mm, "end": v(-109.5, 60) * mm});
            skLineSegment(sketch, "E150.top", {"start": v(-115, 30) * mm, "end": v(-109.5, 30) * mm});
            skLineSegment(sketch, "E150.left", {"start": v(-115, 60) * mm, "end": v(-115, 30) * mm});
            skLineSegment(sketch, "E150.right", {"start": v(-109.5, 60) * mm, "end": v(-109.5, 30) * mm});
            skLineSegment(sketch, "E151.bottom", {"start": v(-115, 120) * mm, "end": v(-109.5, 120) * mm});
            skLineSegment(sketch, "E151.top", {"start": v(-115, 150) * mm, "end": v(-109.5, 150) * mm});
            skLineSegment(sketch, "E151.left", {"start": v(-115, 120) * mm, "end": v(-115, 150) * mm});
            skLineSegment(sketch, "E151.right", {"start": v(-109.5, 120) * mm, "end": v(-109.5, 150) * mm});
            skLineSegment(sketch, "E152.bottom", {"start": v(-140, 150) * mm, "end": v(-170, 150) * mm});
            skLineSegment(sketch, "E152.top", {"start": v(-140, 144.5) * mm, "end": v(-170, 144.5) * mm});
            skLineSegment(sketch, "E152.left", {"start": v(-140, 150) * mm, "end": v(-140, 144.5) * mm});
            skLineSegment(sketch, "E152.right", {"start": v(-170, 150) * mm, "end": v(-170, 144.5) * mm});
            skLineSegment(sketch, "E153.left", {"start": v(-140, 144.5) * mm, "end": v(-140, 144.5) * mm});
            skLineSegment(sketch, "E153.right", {"start": v(-170, 144.5) * mm, "end": v(-170, 144.5) * mm});
            skLineSegment(sketch, "E154.bottom", {"start": v(-40, 150) * mm, "end": v(-80, 150) * mm});
            skLineSegment(sketch, "E154.top", {"start": v(-40, 144.5) * mm, "end": v(-80, 144.5) * mm});
            skLineSegment(sketch, "E154.left", {"start": v(-40, 150) * mm, "end": v(-40, 144.5) * mm});
            skLineSegment(sketch, "E154.right", {"start": v(-80, 150) * mm, "end": v(-80, 144.5) * mm});
            skLineSegment(sketch, "E155.bottom", {"start": v(-16.5, 11) * mm, "end": v(-11, 11) * mm});
            skLineSegment(sketch, "E155.top", {"start": v(-16.5, 16.5) * mm, "end": v(-11, 16.5) * mm});
            skLineSegment(sketch, "E155.left", {"start": v(-16.5, 11) * mm, "end": v(-16.5, 16.5) * mm});
            skLineSegment(sketch, "E155.right", {"start": v(-11, 11) * mm, "end": v(-11, 16.5) * mm});
            skLineSegment(sketch, "E156.bottom", {"start": v(-16.5, 54.5) * mm, "end": v(-11, 54.5) * mm});
            skLineSegment(sketch, "E156.top", {"start": v(-16.5, 49) * mm, "end": v(-11, 49) * mm});
            skLineSegment(sketch, "E156.left", {"start": v(-16.5, 54.5) * mm, "end": v(-16.5, 49) * mm});
            skLineSegment(sketch, "E156.right", {"start": v(-11, 54.5) * mm, "end": v(-11, 49) * mm});
            skLineSegment(sketch, "E157.bottom", {"start": v(-11, 93.5) * mm, "end": v(-16.5, 93.5) * mm});
            skLineSegment(sketch, "E157.top", {"start": v(-11, 99) * mm, "end": v(-16.5, 99) * mm});
            skLineSegment(sketch, "E157.left", {"start": v(-11, 93.5) * mm, "end": v(-11, 99) * mm});
            skLineSegment(sketch, "E157.right", {"start": v(-16.5, 93.5) * mm, "end": v(-16.5, 99) * mm});
            skLineSegment(sketch, "E158.bottom", {"start": v(-11, 139) * mm, "end": v(-16.5, 139) * mm});
            skLineSegment(sketch, "E158.top", {"start": v(-11, 144.5) * mm, "end": v(-16.5, 144.5) * mm});
            skLineSegment(sketch, "E158.left", {"start": v(-11, 139) * mm, "end": v(-11, 144.5) * mm});
            skLineSegment(sketch, "E158.right", {"start": v(-16.5, 139) * mm, "end": v(-16.5, 144.5) * mm});
            skSolve(sketch);
        }
        {
            var Q0;
            Q0 = qSketchRegion(id + "F30", true);
            extrude(context, id + "F31", {"entities" : qUnion([Q0]), "operationType" : NewBodyOperationType.REMOVE, "oppositeDirection" : true, "depth" : 5.5 * mm});
        }
        {
            var Q0;
            Q0=makeQuery(id+"F19.boolean.opBoolean","COPY",FACE,{"derivedFrom":makeQuery(id+"F19.opExtrude","SWEPT_FACE",FACE,{"disambiguationData":[OSD([sQuery(id+"F18.wireOp",EDGE,"E103.top")])]})});
            var sketch = newSketch(context, id + "F32", { "sketchPlane" : qUnion([Q0])});
            skLineSegment(sketch, "E159.bottom", {"start": v(140, 100) * mm, "end": v(170, 100) * mm});
            skLineSegment(sketch, "E159.top", {"start": v(140, 0) * mm, "end": v(170, 0) * mm});
            skLineSegment(sketch, "E159.left", {"start": v(140, 100) * mm, "end": v(140, 0) * mm});
            skLineSegment(sketch, "E159.right", {"start": v(170, 100) * mm, "end": v(170, 0) * mm});
            skSolve(sketch);
        }
        {
            var Q0;
            Q0 = qSketchRegion(id + "F32", true);
            extrude(context, id + "F33", {"entities" : qUnion([Q0]), "depth" : 5.5 * mm});
        }
        {
            var Q0;
            Q0=makeQuery(id+"F19.boolean.opBoolean","COPY",FACE,{"derivedFrom":makeQuery(id+"F19.opExtrude","SWEPT_FACE",FACE,{"disambiguationData":[OSD([sQuery(id+"F18.wireOp",EDGE,"E104.top")])]})});
            var sketch = newSketch(context, id + "F34", { "sketchPlane" : qUnion([Q0])});
            skLineSegment(sketch, "E160.bottom", {"start": v(40, 100) * mm, "end": v(80, 100) * mm});
            skLineSegment(sketch, "E160.top", {"start": v(40, 0) * mm, "end": v(80, 0) * mm});
            skLineSegment(sketch, "E160.left", {"start": v(40, 100) * mm, "end": v(40, 0) * mm});
            skLineSegment(sketch, "E160.right", {"start": v(80, 100) * mm, "end": v(80, 0) * mm});
            skSolve(sketch);
        }
        {
            var Q0;
            Q0 = qSketchRegion(id + "F34", true);
            extrude(context, id + "F35", {"entities" : qUnion([Q0]), "depth" : 5.5 * mm});
        }
        {
            var Q0;
            Q0=makeQuery(id+"F31.boolean.opBoolean","COPY",FACE,{"derivedFrom":makeQuery(id+"F31.opExtrude","SWEPT_FACE",FACE,{"disambiguationData":[OSD([sQuery(id+"F30.wireOp",EDGE,"E151.left")])]})});
            var sketch = newSketch(context, id + "F36", { "sketchPlane" : qUnion([Q0])});
            skLineSegment(sketch, "E161.bottom", {"start": v(150, 34.5) * mm, "end": v(0, 34.5) * mm});
            skLineSegment(sketch, "E161.top", {"start": v(150, 99.5) * mm, "end": v(0, 99.5) * mm});
            skLineSegment(sketch, "E161.left", {"start": v(150, 34.5) * mm, "end": v(150, 99.5) * mm});
            skLineSegment(sketch, "E161.right", {"start": v(0, 34.5) * mm, "end": v(0, 99.5) * mm});
            skSolve(sketch);
        }
        {
            var Q0;
            Q0 = qSketchRegion(id + "F36", true);
            extrude(context, id + "F37", {"entities" : qUnion([Q0]), "depth" : 5.5 * mm});
        }
        {
            var Q0;
            Q0=makeQuery(id+"F37.opExtrude","CAP_FACE",FACE,{"disambiguationData":[OSD([sQuery(id+"F36.wireOp",EDGE,"E161.bottom"),sQuery(id+"F36.wireOp",EDGE,"E161.top"),sQuery(id+"F36.wireOp",EDGE,"E161.left"),sQuery(id+"F36.wireOp",EDGE,"E161.right")])],"isStart":false});
            var sketch = newSketch(context, id + "F38", { "sketchPlane" : qUnion([Q0])});
            skLineSegment(sketch, "E162.bottom", {"start": v(120, 34.5) * mm, "end": v(100, 34.5) * mm});
            skLineSegment(sketch, "E162.top", {"start": v(120, 40) * mm, "end": v(100, 40) * mm});
            skLineSegment(sketch, "E162.left", {"start": v(120, 34.5) * mm, "end": v(120, 40) * mm});
            skLineSegment(sketch, "E162.right", {"start": v(100, 34.5) * mm, "end": v(100, 40) * mm});
            skLineSegment(sketch, "E163.bottom", {"start": v(80, 34.5) * mm, "end": v(60, 34.5) * mm});
            skLineSegment(sketch, "E163.top", {"start": v(80, 40) * mm, "end": v(60, 40) * mm});
            skLineSegment(sketch, "E163.left", {"start": v(80, 34.5) * mm, "end": v(80, 40) * mm});
            skLineSegment(sketch, "E163.right", {"start": v(60, 34.5) * mm, "end": v(60, 40) * mm});
            skLineSegment(sketch, "E164.bottom", {"start": v(30, 34.5) * mm, "end": v(0, 34.5) * mm});
            skLineSegment(sketch, "E164.top", {"start": v(30, 40) * mm, "end": v(0, 40) * mm});
            skLineSegment(sketch, "E164.left", {"start": v(30, 34.5) * mm, "end": v(30, 40) * mm});
            skLineSegment(sketch, "E164.right", {"start": v(0, 34.5) * mm, "end": v(0, 40) * mm});
            skLineSegment(sketch, "E165.bottom", {"start": v(5.5, 99.5) * mm, "end": v(0, 99.5) * mm});
            skLineSegment(sketch, "E165.top", {"start": v(5.5, 79.5) * mm, "end": v(0, 79.5) * mm});
            skLineSegment(sketch, "E165.left", {"start": v(5.5, 99.5) * mm, "end": v(5.5, 79.5) * mm});
            skLineSegment(sketch, "E165.right", {"start": v(0, 99.5) * mm, "end": v(0, 79.5) * mm});
            skLineSegment(sketch, "E166.bottom", {"start": v(5.5, 40) * mm, "end": v(0, 40) * mm});
            skLineSegment(sketch, "E166.top", {"start": v(5.5, 60) * mm, "end": v(0, 60) * mm});
            skLineSegment(sketch, "E166.left", {"start": v(5.5, 40) * mm, "end": v(5.5, 60) * mm});
            skLineSegment(sketch, "E166.right", {"start": v(0, 40) * mm, "end": v(0, 60) * mm});
            skLineSegment(sketch, "E167.bottom", {"start": v(5.5, 99.5) * mm, "end": v(60, 99.5) * mm});
            skLineSegment(sketch, "E167.top", {"start": v(5.5, 94) * mm, "end": v(60, 94) * mm});
            skLineSegment(sketch, "E167.left", {"start": v(5.5, 99.5) * mm, "end": v(5.5, 94) * mm});
            skLineSegment(sketch, "E167.right", {"start": v(60, 99.5) * mm, "end": v(60, 94) * mm});
            skLineSegment(sketch, "E168.bottom", {"start": v(90, 99.5) * mm, "end": v(150, 99.5) * mm});
            skLineSegment(sketch, "E168.top", {"start": v(90, 94) * mm, "end": v(150, 94) * mm});
            skLineSegment(sketch, "E168.left", {"start": v(90, 99.5) * mm, "end": v(90, 94) * mm});
            skLineSegment(sketch, "E168.right", {"start": v(150, 99.5) * mm, "end": v(150, 94) * mm});
            skSolve(sketch);
        }
        {
            var Q0;
            Q0 = qSketchRegion(id + "F38", true);
            extrude(context, id + "F39", {"entities" : qUnion([Q0]), "operationType" : NewBodyOperationType.REMOVE, "oppositeDirection" : true, "depth" : 5.5 * mm});
        }
        {
            var Q0;
            Q0=makeQuery(id+"F31.boolean.opBoolean","COPY",FACE,{"derivedFrom":makeQuery(id+"F31.opExtrude","SWEPT_FACE",FACE,{"disambiguationData":[OSD([sQuery(id+"F30.wireOp",EDGE,"E155.right")])]})});
            var sketch = newSketch(context, id + "F40", { "sketchPlane" : qUnion([Q0])});
            skLineSegment(sketch, "E169.bottom", {"start": v(0, 34.5) * mm, "end": v(-150, 34.5) * mm});
            skLineSegment(sketch, "E169.top", {"start": v(0, 45.5) * mm, "end": v(-150, 45.5) * mm});
            skLineSegment(sketch, "E169.left", {"start": v(0, 34.5) * mm, "end": v(0, 45.5) * mm});
            skLineSegment(sketch, "E169.right", {"start": v(-150, 34.5) * mm, "end": v(-150, 45.5) * mm});
            skSolve(sketch);
        }
        {
            var Q0;
            Q0 = qSketchRegion(id + "F40", true);
            extrude(context, id + "F41", {"entities" : qUnion([Q0]), "depth" : 5.5 * mm});
        }
        {
            var Q0;
            Q0=makeQuery(id+"F41.opExtrude","CAP_FACE",FACE,{"disambiguationData":[OSD([sQuery(id+"F40.wireOp",EDGE,"E169.bottom"),sQuery(id+"F40.wireOp",EDGE,"E169.top"),sQuery(id+"F40.wireOp",EDGE,"E169.left"),sQuery(id+"F40.wireOp",EDGE,"E169.right")])],"isStart":false});
            var sketch = newSketch(context, id + "F42", { "sketchPlane" : qUnion([Q0])});
            skLineSegment(sketch, "E170.bottom", {"start": v(0, 45.5) * mm, "end": v(-5.5, 45.5) * mm});
            skLineSegment(sketch, "E170.top", {"start": v(0, 34.5) * mm, "end": v(-5.5, 34.5) * mm});
            skLineSegment(sketch, "E170.left", {"start": v(0, 45.5) * mm, "end": v(0, 34.5) * mm});
            skLineSegment(sketch, "E170.right", {"start": v(-5.5, 45.5) * mm, "end": v(-5.5, 34.5) * mm});
            skLineSegment(sketch, "E171.bottom", {"start": v(-144.5, 34.5) * mm, "end": v(-150, 34.5) * mm});
            skLineSegment(sketch, "E171.top", {"start": v(-144.5, 40) * mm, "end": v(-150, 40) * mm});
            skLineSegment(sketch, "E171.left", {"start": v(-144.5, 34.5) * mm, "end": v(-144.5, 40) * mm});
            skLineSegment(sketch, "E171.right", {"start": v(-150, 34.5) * mm, "end": v(-150, 40) * mm});
            skLineSegment(sketch, "E172.bottom", {"start": v(-139, 34.5) * mm, "end": v(-99, 34.5) * mm});
            skLineSegment(sketch, "E172.top", {"start": v(-139, 40) * mm, "end": v(-99, 40) * mm});
            skLineSegment(sketch, "E172.left", {"start": v(-139, 34.5) * mm, "end": v(-139, 40) * mm});
            skLineSegment(sketch, "E172.right", {"start": v(-99, 34.5) * mm, "end": v(-99, 40) * mm});
            skLineSegment(sketch, "E173.bottom", {"start": v(-93.5, 34.5) * mm, "end": v(-57, 34.5) * mm});
            skLineSegment(sketch, "E173.top", {"start": v(-93.5, 40) * mm, "end": v(-57, 40) * mm});
            skLineSegment(sketch, "E173.left", {"start": v(-93.5, 34.5) * mm, "end": v(-93.5, 40) * mm});
            skLineSegment(sketch, "E173.right", {"start": v(-57, 34.5) * mm, "end": v(-57, 40) * mm});
            skLineSegment(sketch, "E174.bottom", {"start": v(-51.5, 34.5) * mm, "end": v(-16.5, 34.5) * mm});
            skLineSegment(sketch, "E174.top", {"start": v(-51.5, 40) * mm, "end": v(-16.5, 40) * mm});
            skLineSegment(sketch, "E174.left", {"start": v(-51.5, 34.5) * mm, "end": v(-51.5, 40) * mm});
            skLineSegment(sketch, "E174.right", {"start": v(-16.5, 34.5) * mm, "end": v(-16.5, 40) * mm});
            skLineSegment(sketch, "E175.bottom", {"start": v(-11, 34.5) * mm, "end": v(-5.5, 34.5) * mm});
            skLineSegment(sketch, "E175.top", {"start": v(-11, 40) * mm, "end": v(-5.5, 40) * mm});
            skLineSegment(sketch, "E175.left", {"start": v(-11, 34.5) * mm, "end": v(-11, 40) * mm});
            skLineSegment(sketch, "E175.right", {"start": v(-5.5, 34.5) * mm, "end": v(-5.5, 40) * mm});
            skSolve(sketch);
        }
        {
            var Q0;
            Q0 = qSketchRegion(id + "F42", true);
            extrude(context, id + "F43", {"entities" : qUnion([Q0]), "operationType" : NewBodyOperationType.REMOVE, "oppositeDirection" : true, "depth" : 5.5 * mm});
        }
        {
            var Q0;
            Q0=makeQuery(id+"F3.boolean.opBoolean","COPY",FACE,{"derivedFrom":makeQuery(id+"F3.opExtrude","SWEPT_FACE",FACE,{"disambiguationData":[OSD([sQuery(id+"F2.wireOp",EDGE,"E23.right")])]})});
            var sketch = newSketch(context, id + "F44", { "sketchPlane" : qUnion([Q0])});
            skLineSegment(sketch, "E176.bottom", {"start": v(-27.5, 0) * mm, "end": v(-7.5, 0) * mm});
            skLineSegment(sketch, "E176.top", {"start": v(-27.5, 11) * mm, "end": v(-7.5, 11) * mm});
            skLineSegment(sketch, "E176.left", {"start": v(-27.5, 0) * mm, "end": v(-27.5, 11) * mm});
            skLineSegment(sketch, "E176.right", {"start": v(-7.5, 0) * mm, "end": v(-7.5, 11) * mm});
            skSolve(sketch);
        }
        {
            var Q0;
            Q0 = qSketchRegion(id + "F44", true);
            extrude(context, id + "F45", {"entities" : qUnion([Q0]), "depth" : 5.5 * mm});
        }
        {
            var Q0;
            Q0=makeQuery(id+"F45.opExtrude","CAP_FACE",FACE,{"disambiguationData":[OSD([sQuery(id+"F44.wireOp",EDGE,"E176.bottom"),sQuery(id+"F44.wireOp",EDGE,"E176.top"),sQuery(id+"F44.wireOp",EDGE,"E176.left"),sQuery(id+"F44.wireOp",EDGE,"E176.right")])],"isStart":false});
            var sketch = newSketch(context, id + "F46", { "sketchPlane" : qUnion([Q0])});
            skLineSegment(sketch, "E177.bottom", {"start": v(-27.5, 0) * mm, "end": v(-22, 0) * mm});
            skLineSegment(sketch, "E177.top", {"start": v(-27.5, 5.5) * mm, "end": v(-22, 5.5) * mm});
            skLineSegment(sketch, "E177.left", {"start": v(-27.5, 0) * mm, "end": v(-27.5, 5.5) * mm});
            skLineSegment(sketch, "E177.right", {"start": v(-22, 0) * mm, "end": v(-22, 5.5) * mm});
            skLineSegment(sketch, "E178.bottom", {"start": v(-7.5, 0) * mm, "end": v(-13, 0) * mm});
            skLineSegment(sketch, "E178.top", {"start": v(-7.5, 5.5) * mm, "end": v(-13, 5.5) * mm});
            skLineSegment(sketch, "E178.left", {"start": v(-7.5, 0) * mm, "end": v(-7.5, 5.5) * mm});
            skLineSegment(sketch, "E178.right", {"start": v(-13, 0) * mm, "end": v(-13, 5.5) * mm});
            skSolve(sketch);
        }
        {
            var Q0;
            Q0 = qSketchRegion(id + "F46", true);
            extrude(context, id + "F47", {"entities" : qUnion([Q0]), "operationType" : NewBodyOperationType.REMOVE, "oppositeDirection" : true, "depth" : 5.5 * mm});
        }
        {
            var Q0;
            Q0=makeQuery(id+"F3.boolean.opBoolean","COPY",FACE,{"derivedFrom":makeQuery(id+"F3.opExtrude","SWEPT_FACE",FACE,{"disambiguationData":[OSD([sQuery(id+"F2.wireOp",EDGE,"E22.right")])]})});
            var sketch = newSketch(context, id + "F48", { "sketchPlane" : qUnion([Q0])});
            skLineSegment(sketch, "E179.bottom", {"start": v(-150, 0) * mm, "end": v(-75.5, 0) * mm});
            skLineSegment(sketch, "E179.top", {"start": v(-150, 11) * mm, "end": v(-75.5, 11) * mm});
            skLineSegment(sketch, "E179.left", {"start": v(-150, 0) * mm, "end": v(-150, 11) * mm});
            skLineSegment(sketch, "E179.right", {"start": v(-75.5, 0) * mm, "end": v(-75.5, 11) * mm});
            skSolve(sketch);
        }
        {
            var Q0;
            Q0 = qSketchRegion(id + "F48", true);
            extrude(context, id + "F49", {"entities" : qUnion([Q0]), "depth" : 5 * mm});
        }
        {
            var Q0;
            Q0=makeQuery(id+"F49.opExtrude","CAP_FACE",FACE,{"disambiguationData":[OSD([sQuery(id+"F48.wireOp",EDGE,"E179.bottom"),sQuery(id+"F48.wireOp",EDGE,"E179.top"),sQuery(id+"F48.wireOp",EDGE,"E179.left"),sQuery(id+"F48.wireOp",EDGE,"E179.right")])],"isStart":true});
            var sketch = newSketch(context, id + "F50", { "sketchPlane" : qUnion([Q0])});
            skLineSegment(sketch, "E180.bottom", {"start": v(75.5, 0) * mm, "end": v(86.5, 0) * mm});
            skLineSegment(sketch, "E180.top", {"start": v(75.5, 5.5) * mm, "end": v(86.5, 5.5) * mm});
            skLineSegment(sketch, "E180.left", {"start": v(75.5, 0) * mm, "end": v(75.5, 5.5) * mm});
            skLineSegment(sketch, "E180.right", {"start": v(86.5, 0) * mm, "end": v(86.5, 5.5) * mm});
            skLineSegment(sketch, "E181.bottom", {"start": v(97.5, 0) * mm, "end": v(119, 0) * mm});
            skLineSegment(sketch, "E181.top", {"start": v(97.5, 5.5) * mm, "end": v(119, 5.5) * mm});
            skLineSegment(sketch, "E181.left", {"start": v(97.5, 0) * mm, "end": v(97.5, 5.5) * mm});
            skLineSegment(sketch, "E181.right", {"start": v(119, 0) * mm, "end": v(119, 5.5) * mm});
            skLineSegment(sketch, "E182.bottom", {"start": v(130, 0) * mm, "end": v(150, 0) * mm});
            skLineSegment(sketch, "E182.top", {"start": v(130, 5.5) * mm, "end": v(150, 5.5) * mm});
            skLineSegment(sketch, "E182.left", {"start": v(130, 0) * mm, "end": v(130, 5.5) * mm});
            skLineSegment(sketch, "E182.right", {"start": v(150, 0) * mm, "end": v(150, 5.5) * mm});
            skSolve(sketch);
        }
        {
            var Q0;
            Q0 = qSketchRegion(id + "F50", true);
            extrude(context, id + "F51", {"entities" : qUnion([Q0]), "operationType" : NewBodyOperationType.REMOVE, "oppositeDirection" : true, "depth" : 5.5 * mm});
        }
    });
